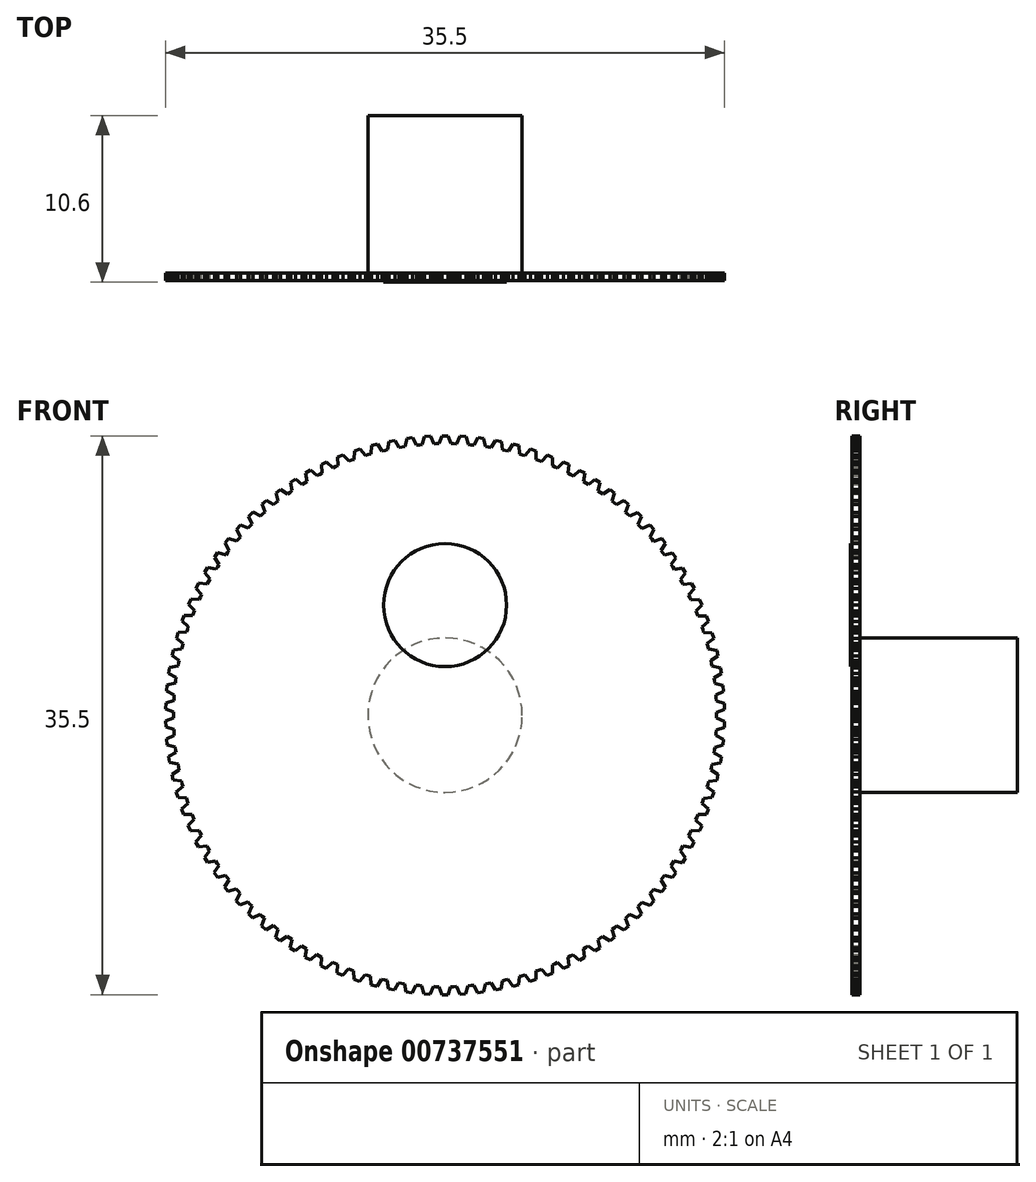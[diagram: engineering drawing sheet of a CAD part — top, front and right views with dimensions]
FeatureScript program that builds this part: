
annotation { "Feature Type Name" : "Feature", "Feature Type Description" : "" }
export const myFeature = defineFeature(function(context is Context, id is Id, definition is map)
    precondition{}
    {
        {
            var Q0;
            Q0=qCreatedBy(makeId("Front.planeOp"),FACE);
            var sketch = newSketch(context, id + "F0", { "sketchPlane" : qUnion([Q0])});
            skLineSegment(sketch, "E0", {"start": v(0, 0) * mm, "end": v(0, 17.75) * mm, "construction": true});
            skCircle(sketch, "E1.0", {"center": v(-0.16, 0) * mm, "radius": 17.25 * mm, "construction": true});
            skLineSegment(sketch, "E2", {"start": v(0, 17.75) * mm, "end": v(-0.19, 17.75) * mm});
            skLineSegment(sketch, "E3", {"start": v(-0.19, 17.75) * mm, "end": v(-0.37, 17.25) * mm});
            skLineSegment(sketch, "E4", {"start": v(-0.37, 17.25) * mm, "end": v(-0.56, 17.24) * mm});
            skLineSegment(sketch, "E5.MirrorCS", {"start": v(0.19, 17.75) * mm, "end": v(0.37, 17.25) * mm});
            skLineSegment(sketch, "E6.MirrorCS", {"start": v(0.37, 17.25) * mm, "end": v(0.56, 17.24) * mm});
            skLineSegment(sketch, "E7.MirrorCS", {"start": v(0, 17.75) * mm, "end": v(0.19, 17.75) * mm});
            skLineSegment(sketch, "E8.1.0", {"start": v(0.95, 17.73) * mm, "end": v(0.73, 17.23) * mm});
            skLineSegment(sketch, "E8.1.1", {"start": v(1.32, 17.7) * mm, "end": v(1.48, 17.19) * mm});
            skLineSegment(sketch, "E8.1.2", {"start": v(1.48, 17.19) * mm, "end": v(1.66, 17.17) * mm});
            skLineSegment(sketch, "E8.1.3", {"start": v(0.73, 17.23) * mm, "end": v(0.55, 17.24) * mm});
            skLineSegment(sketch, "E8.1.4", {"start": v(1.14, 17.71) * mm, "end": v(1.32, 17.7) * mm});
            skLineSegment(sketch, "E8.1.5", {"start": v(1.14, 17.71) * mm, "end": v(0.95, 17.73) * mm});
            skLineSegment(sketch, "E8.2.0", {"start": v(2.09, 17.63) * mm, "end": v(1.84, 17.15) * mm});
            skLineSegment(sketch, "E8.2.1", {"start": v(2.45, 17.58) * mm, "end": v(2.57, 17.06) * mm});
            skLineSegment(sketch, "E8.2.2", {"start": v(2.57, 17.06) * mm, "end": v(2.76, 17.03) * mm});
            skLineSegment(sketch, "E8.2.3", {"start": v(1.84, 17.15) * mm, "end": v(1.65, 17.17) * mm});
            skLineSegment(sketch, "E8.2.4", {"start": v(2.27, 17.6) * mm, "end": v(2.45, 17.58) * mm});
            skLineSegment(sketch, "E8.2.5", {"start": v(2.27, 17.6) * mm, "end": v(2.09, 17.63) * mm});
            skLineSegment(sketch, "E8.3.0", {"start": v(3.21, 17.46) * mm, "end": v(2.93, 17) * mm});
            skLineSegment(sketch, "E8.3.1", {"start": v(3.58, 17.39) * mm, "end": v(3.66, 16.86) * mm});
            skLineSegment(sketch, "E8.3.2", {"start": v(3.66, 16.86) * mm, "end": v(3.84, 16.82) * mm});
            skLineSegment(sketch, "E8.3.3", {"start": v(2.93, 17) * mm, "end": v(2.75, 17.03) * mm});
            skLineSegment(sketch, "E8.3.4", {"start": v(3.4, 17.42) * mm, "end": v(3.58, 17.39) * mm});
            skLineSegment(sketch, "E8.3.5", {"start": v(3.4, 17.42) * mm, "end": v(3.21, 17.46) * mm});
            skLineSegment(sketch, "E8.4.0", {"start": v(4.32, 17.22) * mm, "end": v(4.02, 16.78) * mm});
            skLineSegment(sketch, "E8.4.1", {"start": v(4.68, 17.12) * mm, "end": v(4.73, 16.59) * mm});
            skLineSegment(sketch, "E8.4.2", {"start": v(4.73, 16.59) * mm, "end": v(4.91, 16.54) * mm});
            skLineSegment(sketch, "E8.4.3", {"start": v(4.02, 16.78) * mm, "end": v(3.84, 16.82) * mm});
            skLineSegment(sketch, "E8.4.4", {"start": v(4.5, 17.17) * mm, "end": v(4.68, 17.12) * mm});
            skLineSegment(sketch, "E8.4.5", {"start": v(4.5, 17.17) * mm, "end": v(4.32, 17.22) * mm});
            skLineSegment(sketch, "E8.5.0", {"start": v(5.42, 16.9) * mm, "end": v(5.08, 16.48) * mm});
            skLineSegment(sketch, "E8.5.1", {"start": v(5.77, 16.79) * mm, "end": v(5.79, 16.25) * mm});
            skLineSegment(sketch, "E8.5.2", {"start": v(5.79, 16.25) * mm, "end": v(5.96, 16.19) * mm});
            skLineSegment(sketch, "E8.5.3", {"start": v(5.08, 16.48) * mm, "end": v(4.9, 16.54) * mm});
            skLineSegment(sketch, "E8.5.4", {"start": v(5.6, 16.85) * mm, "end": v(5.77, 16.79) * mm});
            skLineSegment(sketch, "E8.5.5", {"start": v(5.6, 16.85) * mm, "end": v(5.42, 16.9) * mm});
            skLineSegment(sketch, "E8.6.0", {"start": v(6.5, 16.52) * mm, "end": v(6.13, 16.12) * mm});
            skLineSegment(sketch, "E8.6.1", {"start": v(6.83, 16.38) * mm, "end": v(6.82, 15.85) * mm});
            skLineSegment(sketch, "E8.6.2", {"start": v(6.82, 15.85) * mm, "end": v(6.99, 15.77) * mm});
            skLineSegment(sketch, "E8.6.3", {"start": v(6.13, 16.12) * mm, "end": v(5.96, 16.2) * mm});
            skLineSegment(sketch, "E8.6.4", {"start": v(6.66, 16.45) * mm, "end": v(6.83, 16.38) * mm});
            skLineSegment(sketch, "E8.6.5", {"start": v(6.66, 16.45) * mm, "end": v(6.5, 16.52) * mm});
            skLineSegment(sketch, "E8.7.0", {"start": v(7.54, 16.07) * mm, "end": v(7.15, 15.7) * mm});
            skLineSegment(sketch, "E8.7.1", {"start": v(7.87, 15.91) * mm, "end": v(7.82, 15.38) * mm});
            skLineSegment(sketch, "E8.7.2", {"start": v(7.82, 15.38) * mm, "end": v(7.99, 15.3) * mm});
            skLineSegment(sketch, "E8.7.3", {"start": v(7.15, 15.7) * mm, "end": v(6.98, 15.78) * mm});
            skLineSegment(sketch, "E8.7.4", {"start": v(7.7, 16) * mm, "end": v(7.87, 15.91) * mm});
            skLineSegment(sketch, "E8.7.5", {"start": v(7.7, 16) * mm, "end": v(7.54, 16.07) * mm});
            skLineSegment(sketch, "E8.8.0", {"start": v(8.55, 15.56) * mm, "end": v(8.14, 15.2) * mm});
            skLineSegment(sketch, "E8.8.1", {"start": v(8.87, 15.37) * mm, "end": v(8.79, 14.84) * mm});
            skLineSegment(sketch, "E8.8.2", {"start": v(8.79, 14.84) * mm, "end": v(8.95, 14.75) * mm});
            skLineSegment(sketch, "E8.8.3", {"start": v(8.14, 15.2) * mm, "end": v(7.98, 15.3) * mm});
            skLineSegment(sketch, "E8.8.4", {"start": v(8.71, 15.46) * mm, "end": v(8.87, 15.37) * mm});
            skLineSegment(sketch, "E8.8.5", {"start": v(8.71, 15.46) * mm, "end": v(8.55, 15.56) * mm});
            skLineSegment(sketch, "E8.9.0", {"start": v(9.53, 14.98) * mm, "end": v(9.1, 14.66) * mm});
            skLineSegment(sketch, "E8.9.1", {"start": v(9.84, 14.77) * mm, "end": v(9.72, 14.25) * mm});
            skLineSegment(sketch, "E8.9.2", {"start": v(9.72, 14.25) * mm, "end": v(9.88, 14.15) * mm});
            skLineSegment(sketch, "E8.9.3", {"start": v(9.1, 14.66) * mm, "end": v(8.94, 14.75) * mm});
            skLineSegment(sketch, "E8.9.4", {"start": v(9.69, 14.87) * mm, "end": v(9.84, 14.77) * mm});
            skLineSegment(sketch, "E8.9.5", {"start": v(9.69, 14.87) * mm, "end": v(9.53, 14.98) * mm});
            skLineSegment(sketch, "E8.10.0", {"start": v(10.47, 14.33) * mm, "end": v(10.02, 14.04) * mm});
            skLineSegment(sketch, "E8.10.1", {"start": v(10.77, 14.11) * mm, "end": v(10.61, 13.6) * mm});
            skLineSegment(sketch, "E8.10.2", {"start": v(10.61, 13.6) * mm, "end": v(10.76, 13.48) * mm});
            skLineSegment(sketch, "E8.10.3", {"start": v(10.02, 14.04) * mm, "end": v(9.87, 14.15) * mm});
            skLineSegment(sketch, "E8.10.4", {"start": v(10.62, 14.22) * mm, "end": v(10.77, 14.11) * mm});
            skLineSegment(sketch, "E8.10.5", {"start": v(10.62, 14.22) * mm, "end": v(10.47, 14.33) * mm});
            skLineSegment(sketch, "E8.11.0", {"start": v(11.37, 13.63) * mm, "end": v(10.9, 13.37) * mm});
            skLineSegment(sketch, "E8.11.1", {"start": v(11.65, 13.4) * mm, "end": v(11.46, 12.89) * mm});
            skLineSegment(sketch, "E8.11.2", {"start": v(11.46, 12.89) * mm, "end": v(11.6, 12.77) * mm});
            skLineSegment(sketch, "E8.11.3", {"start": v(10.9, 13.37) * mm, "end": v(10.75, 13.49) * mm});
            skLineSegment(sketch, "E8.11.4", {"start": v(11.5, 13.51) * mm, "end": v(11.65, 13.4) * mm});
            skLineSegment(sketch, "E8.11.5", {"start": v(11.5, 13.51) * mm, "end": v(11.37, 13.63) * mm});
            skLineSegment(sketch, "E8.12.0", {"start": v(12.22, 12.88) * mm, "end": v(11.73, 12.65) * mm});
            skLineSegment(sketch, "E8.12.1", {"start": v(12.48, 12.62) * mm, "end": v(12.27, 12.13) * mm});
            skLineSegment(sketch, "E8.12.2", {"start": v(12.27, 12.13) * mm, "end": v(12.4, 12) * mm});
            skLineSegment(sketch, "E8.12.3", {"start": v(11.73, 12.65) * mm, "end": v(11.6, 12.77) * mm});
            skLineSegment(sketch, "E8.12.4", {"start": v(12.35, 12.75) * mm, "end": v(12.48, 12.62) * mm});
            skLineSegment(sketch, "E8.12.5", {"start": v(12.35, 12.75) * mm, "end": v(12.22, 12.88) * mm});
            skLineSegment(sketch, "E8.13.0", {"start": v(13.02, 12.07) * mm, "end": v(12.52, 11.87) * mm});
            skLineSegment(sketch, "E8.13.1", {"start": v(13.27, 11.8) * mm, "end": v(13.02, 11.32) * mm});
            skLineSegment(sketch, "E8.13.2", {"start": v(13.02, 11.32) * mm, "end": v(13.14, 11.18) * mm});
            skLineSegment(sketch, "E8.13.3", {"start": v(12.52, 11.87) * mm, "end": v(12.4, 12) * mm});
            skLineSegment(sketch, "E8.13.4", {"start": v(13.14, 11.93) * mm, "end": v(13.27, 11.8) * mm});
            skLineSegment(sketch, "E8.13.5", {"start": v(13.14, 11.93) * mm, "end": v(13.02, 12.07) * mm});
            skLineSegment(sketch, "E8.14.0", {"start": v(13.76, 11.2) * mm, "end": v(13.25, 11.04) * mm});
            skLineSegment(sketch, "E8.14.1", {"start": v(14, 10.92) * mm, "end": v(13.72, 10.46) * mm});
            skLineSegment(sketch, "E8.14.2", {"start": v(13.72, 10.46) * mm, "end": v(13.83, 10.31) * mm});
            skLineSegment(sketch, "E8.14.3", {"start": v(13.25, 11.04) * mm, "end": v(13.14, 11.18) * mm});
            skLineSegment(sketch, "E8.14.4", {"start": v(13.88, 11.06) * mm, "end": v(14, 10.92) * mm});
            skLineSegment(sketch, "E8.14.5", {"start": v(13.88, 11.06) * mm, "end": v(13.76, 11.2) * mm});
            skLineSegment(sketch, "E8.15.0", {"start": v(14.45, 10.3) * mm, "end": v(13.93, 10.17) * mm});
            skLineSegment(sketch, "E8.15.1", {"start": v(14.67, 10) * mm, "end": v(14.36, 9.56) * mm});
            skLineSegment(sketch, "E8.15.2", {"start": v(14.36, 9.56) * mm, "end": v(14.46, 9.4) * mm});
            skLineSegment(sketch, "E8.15.3", {"start": v(13.93, 10.17) * mm, "end": v(13.82, 10.32) * mm});
            skLineSegment(sketch, "E8.15.4", {"start": v(14.56, 10.15) * mm, "end": v(14.67, 10) * mm});
            skLineSegment(sketch, "E8.15.5", {"start": v(14.56, 10.15) * mm, "end": v(14.45, 10.3) * mm});
            skLineSegment(sketch, "E8.16.0", {"start": v(15.08, 9.36) * mm, "end": v(14.56, 9.26) * mm});
            skLineSegment(sketch, "E8.16.1", {"start": v(15.28, 9.04) * mm, "end": v(14.94, 8.62) * mm});
            skLineSegment(sketch, "E8.16.2", {"start": v(14.94, 8.62) * mm, "end": v(15.04, 8.46) * mm});
            skLineSegment(sketch, "E8.16.3", {"start": v(14.56, 9.26) * mm, "end": v(14.46, 9.41) * mm});
            skLineSegment(sketch, "E8.16.4", {"start": v(15.18, 9.2) * mm, "end": v(15.28, 9.04) * mm});
            skLineSegment(sketch, "E8.16.5", {"start": v(15.18, 9.2) * mm, "end": v(15.08, 9.36) * mm});
            skLineSegment(sketch, "E8.17.0", {"start": v(15.65, 8.37) * mm, "end": v(15.12, 8.3) * mm});
            skLineSegment(sketch, "E8.17.1", {"start": v(15.82, 8.04) * mm, "end": v(15.46, 7.64) * mm});
            skLineSegment(sketch, "E8.17.2", {"start": v(15.46, 7.64) * mm, "end": v(15.55, 7.48) * mm});
            skLineSegment(sketch, "E8.17.3", {"start": v(15.12, 8.3) * mm, "end": v(15.03, 8.47) * mm});
            skLineSegment(sketch, "E8.17.4", {"start": v(15.74, 8.2) * mm, "end": v(15.82, 8.04) * mm});
            skLineSegment(sketch, "E8.17.5", {"start": v(15.74, 8.2) * mm, "end": v(15.65, 8.37) * mm});
            skLineSegment(sketch, "E8.18.0", {"start": v(16.16, 7.35) * mm, "end": v(15.62, 7.32) * mm});
            skLineSegment(sketch, "E8.18.1", {"start": v(16.3, 7.01) * mm, "end": v(15.92, 6.64) * mm});
            skLineSegment(sketch, "E8.18.2", {"start": v(15.92, 6.64) * mm, "end": v(16, 6.47) * mm});
            skLineSegment(sketch, "E8.18.3", {"start": v(15.62, 7.32) * mm, "end": v(15.54, 7.49) * mm});
            skLineSegment(sketch, "E8.18.4", {"start": v(16.23, 7.18) * mm, "end": v(16.3, 7.01) * mm});
            skLineSegment(sketch, "E8.18.5", {"start": v(16.23, 7.18) * mm, "end": v(16.16, 7.35) * mm});
            skLineSegment(sketch, "E8.19.0", {"start": v(16.6, 6.3) * mm, "end": v(16.06, 6.3) * mm});
            skLineSegment(sketch, "E8.19.1", {"start": v(16.72, 5.95) * mm, "end": v(16.31, 5.6) * mm});
            skLineSegment(sketch, "E8.19.2", {"start": v(16.31, 5.6) * mm, "end": v(16.38, 5.43) * mm});
            skLineSegment(sketch, "E8.19.3", {"start": v(16.06, 6.3) * mm, "end": v(16, 6.47) * mm});
            skLineSegment(sketch, "E8.19.4", {"start": v(16.66, 6.13) * mm, "end": v(16.72, 5.95) * mm});
            skLineSegment(sketch, "E8.19.5", {"start": v(16.66, 6.13) * mm, "end": v(16.6, 6.3) * mm});
            skLineSegment(sketch, "E8.20.0", {"start": v(16.96, 5.22) * mm, "end": v(16.43, 5.26) * mm});
            skLineSegment(sketch, "E8.20.1", {"start": v(17.07, 4.87) * mm, "end": v(16.64, 4.55) * mm});
            skLineSegment(sketch, "E8.20.2", {"start": v(16.64, 4.55) * mm, "end": v(16.69, 4.37) * mm});
            skLineSegment(sketch, "E8.20.3", {"start": v(16.43, 5.26) * mm, "end": v(16.37, 5.44) * mm});
            skLineSegment(sketch, "E8.20.4", {"start": v(17.02, 5.05) * mm, "end": v(17.07, 4.87) * mm});
            skLineSegment(sketch, "E8.20.5", {"start": v(17.02, 5.05) * mm, "end": v(16.96, 5.22) * mm});
            skLineSegment(sketch, "E8.21.0", {"start": v(17.26, 4.13) * mm, "end": v(16.73, 4.2) * mm});
            skLineSegment(sketch, "E8.21.1", {"start": v(17.35, 3.76) * mm, "end": v(16.9, 3.47) * mm});
            skLineSegment(sketch, "E8.21.2", {"start": v(16.9, 3.47) * mm, "end": v(16.94, 3.29) * mm});
            skLineSegment(sketch, "E8.21.3", {"start": v(16.73, 4.2) * mm, "end": v(16.69, 4.38) * mm});
            skLineSegment(sketch, "E8.21.4", {"start": v(17.3, 3.94) * mm, "end": v(17.35, 3.76) * mm});
            skLineSegment(sketch, "E8.21.5", {"start": v(17.3, 3.94) * mm, "end": v(17.26, 4.13) * mm});
            skLineSegment(sketch, "E8.22.0", {"start": v(17.5, 3.01) * mm, "end": v(16.97, 3.11) * mm});
            skLineSegment(sketch, "E8.22.1", {"start": v(17.55, 2.64) * mm, "end": v(17.08, 2.38) * mm});
            skLineSegment(sketch, "E8.22.2", {"start": v(17.08, 2.38) * mm, "end": v(17.11, 2.2) * mm});
            skLineSegment(sketch, "E8.22.3", {"start": v(16.97, 3.11) * mm, "end": v(16.93, 3.3) * mm});
            skLineSegment(sketch, "E8.22.4", {"start": v(17.52, 2.83) * mm, "end": v(17.55, 2.64) * mm});
            skLineSegment(sketch, "E8.22.5", {"start": v(17.52, 2.83) * mm, "end": v(17.5, 3.01) * mm});
            skLineSegment(sketch, "E8.23.0", {"start": v(17.65, 1.88) * mm, "end": v(17.13, 2.02) * mm});
            skLineSegment(sketch, "E8.23.1", {"start": v(17.69, 1.51) * mm, "end": v(17.2, 1.28) * mm});
            skLineSegment(sketch, "E8.23.2", {"start": v(17.2, 1.28) * mm, "end": v(17.22, 1.1) * mm});
            skLineSegment(sketch, "E8.23.3", {"start": v(17.13, 2.02) * mm, "end": v(17.11, 2.2) * mm});
            skLineSegment(sketch, "E8.23.4", {"start": v(17.67, 1.7) * mm, "end": v(17.69, 1.51) * mm});
            skLineSegment(sketch, "E8.23.5", {"start": v(17.67, 1.7) * mm, "end": v(17.65, 1.88) * mm});
            skLineSegment(sketch, "E8.24.0", {"start": v(17.74, 0.75) * mm, "end": v(17.23, 0.92) * mm});
            skLineSegment(sketch, "E8.24.1", {"start": v(17.75, 0.38) * mm, "end": v(17.25, 0.18) * mm});
            skLineSegment(sketch, "E8.24.2", {"start": v(17.25, 0.18) * mm, "end": v(17.25, -0.01) * mm});
            skLineSegment(sketch, "E8.24.3", {"start": v(17.23, 0.92) * mm, "end": v(17.22, 1.1) * mm});
            skLineSegment(sketch, "E8.24.4", {"start": v(17.74, 0.56) * mm, "end": v(17.75, 0.38) * mm});
            skLineSegment(sketch, "E8.24.5", {"start": v(17.74, 0.56) * mm, "end": v(17.74, 0.75) * mm});
            skLineSegment(sketch, "E8.25.0", {"start": v(17.75, -0.39) * mm, "end": v(17.25, -0.19) * mm});
            skLineSegment(sketch, "E8.25.1", {"start": v(17.73, -0.76) * mm, "end": v(17.22, -0.93) * mm});
            skLineSegment(sketch, "E8.25.2", {"start": v(17.22, -0.93) * mm, "end": v(17.22, -1.12) * mm});
            skLineSegment(sketch, "E8.25.3", {"start": v(17.25, -0.19) * mm, "end": v(17.25, 0) * mm});
            skLineSegment(sketch, "E8.25.4", {"start": v(17.74, -0.57) * mm, "end": v(17.73, -0.76) * mm});
            skLineSegment(sketch, "E8.25.5", {"start": v(17.74, -0.57) * mm, "end": v(17.75, -0.39) * mm});
            skLineSegment(sketch, "E8.26.0", {"start": v(17.69, -1.53) * mm, "end": v(17.2, -1.3) * mm});
            skLineSegment(sketch, "E8.26.1", {"start": v(17.65, -1.9) * mm, "end": v(17.13, -2.03) * mm});
            skLineSegment(sketch, "E8.26.2", {"start": v(17.13, -2.03) * mm, "end": v(17.1, -2.22) * mm});
            skLineSegment(sketch, "E8.26.3", {"start": v(17.2, -1.3) * mm, "end": v(17.22, -1.1) * mm});
            skLineSegment(sketch, "E8.26.4", {"start": v(17.67, -1.71) * mm, "end": v(17.65, -1.9) * mm});
            skLineSegment(sketch, "E8.26.5", {"start": v(17.67, -1.71) * mm, "end": v(17.69, -1.53) * mm});
            skLineSegment(sketch, "E8.27.0", {"start": v(17.55, -2.66) * mm, "end": v(17.08, -2.4) * mm});
            skLineSegment(sketch, "E8.27.1", {"start": v(17.5, -3.02) * mm, "end": v(16.96, -3.13) * mm});
            skLineSegment(sketch, "E8.27.2", {"start": v(16.96, -3.13) * mm, "end": v(16.93, -3.3) * mm});
            skLineSegment(sketch, "E8.27.3", {"start": v(17.08, -2.4) * mm, "end": v(17.1, -2.2) * mm});
            skLineSegment(sketch, "E8.27.4", {"start": v(17.52, -2.84) * mm, "end": v(17.5, -3.02) * mm});
            skLineSegment(sketch, "E8.27.5", {"start": v(17.52, -2.84) * mm, "end": v(17.55, -2.66) * mm});
            skLineSegment(sketch, "E8.28.0", {"start": v(17.34, -3.77) * mm, "end": v(16.9, -3.48) * mm});
            skLineSegment(sketch, "E8.28.1", {"start": v(17.26, -4.14) * mm, "end": v(16.73, -4.2) * mm});
            skLineSegment(sketch, "E8.28.2", {"start": v(16.73, -4.2) * mm, "end": v(16.68, -4.39) * mm});
            skLineSegment(sketch, "E8.28.3", {"start": v(16.9, -3.48) * mm, "end": v(16.93, -3.3) * mm});
            skLineSegment(sketch, "E8.28.4", {"start": v(17.3, -3.96) * mm, "end": v(17.26, -4.14) * mm});
            skLineSegment(sketch, "E8.28.5", {"start": v(17.3, -3.96) * mm, "end": v(17.34, -3.77) * mm});
            skLineSegment(sketch, "E8.29.0", {"start": v(17.07, -4.88) * mm, "end": v(16.64, -4.56) * mm});
            skLineSegment(sketch, "E8.29.1", {"start": v(16.96, -5.24) * mm, "end": v(16.43, -5.27) * mm});
            skLineSegment(sketch, "E8.29.2", {"start": v(16.43, -5.27) * mm, "end": v(16.37, -5.45) * mm});
            skLineSegment(sketch, "E8.29.3", {"start": v(16.64, -4.56) * mm, "end": v(16.69, -4.38) * mm});
            skLineSegment(sketch, "E8.29.4", {"start": v(17.01, -5.06) * mm, "end": v(16.96, -5.24) * mm});
            skLineSegment(sketch, "E8.29.5", {"start": v(17.01, -5.06) * mm, "end": v(17.07, -4.88) * mm});
            skLineSegment(sketch, "E8.30.0", {"start": v(16.72, -5.96) * mm, "end": v(16.31, -5.61) * mm});
            skLineSegment(sketch, "E8.30.1", {"start": v(16.6, -6.31) * mm, "end": v(16.05, -6.31) * mm});
            skLineSegment(sketch, "E8.30.2", {"start": v(16.05, -6.31) * mm, "end": v(15.99, -6.48) * mm});
            skLineSegment(sketch, "E8.30.3", {"start": v(16.31, -5.61) * mm, "end": v(16.37, -5.44) * mm});
            skLineSegment(sketch, "E8.30.4", {"start": v(16.66, -6.14) * mm, "end": v(16.6, -6.31) * mm});
            skLineSegment(sketch, "E8.30.5", {"start": v(16.66, -6.14) * mm, "end": v(16.72, -5.96) * mm});
            skLineSegment(sketch, "E8.31.0", {"start": v(16.3, -7.02) * mm, "end": v(15.92, -6.65) * mm});
            skLineSegment(sketch, "E8.31.1", {"start": v(16.15, -7.36) * mm, "end": v(15.62, -7.33) * mm});
            skLineSegment(sketch, "E8.31.2", {"start": v(15.62, -7.33) * mm, "end": v(15.54, -7.5) * mm});
            skLineSegment(sketch, "E8.31.3", {"start": v(15.92, -6.65) * mm, "end": v(15.99, -6.48) * mm});
            skLineSegment(sketch, "E8.31.4", {"start": v(16.23, -7.2) * mm, "end": v(16.15, -7.36) * mm});
            skLineSegment(sketch, "E8.31.5", {"start": v(16.23, -7.2) * mm, "end": v(16.3, -7.02) * mm});
            skLineSegment(sketch, "E8.32.0", {"start": v(15.82, -8.05) * mm, "end": v(15.46, -7.65) * mm});
            skLineSegment(sketch, "E8.32.1", {"start": v(15.65, -8.38) * mm, "end": v(15.11, -8.31) * mm});
            skLineSegment(sketch, "E8.32.2", {"start": v(15.11, -8.31) * mm, "end": v(15.03, -8.48) * mm});
            skLineSegment(sketch, "E8.32.3", {"start": v(15.46, -7.65) * mm, "end": v(15.54, -7.49) * mm});
            skLineSegment(sketch, "E8.32.4", {"start": v(15.73, -8.22) * mm, "end": v(15.65, -8.38) * mm});
            skLineSegment(sketch, "E8.32.5", {"start": v(15.73, -8.22) * mm, "end": v(15.82, -8.05) * mm});
            skLineSegment(sketch, "E8.33.0", {"start": v(15.27, -9.05) * mm, "end": v(14.94, -8.63) * mm});
            skLineSegment(sketch, "E8.33.1", {"start": v(15.08, -9.37) * mm, "end": v(14.55, -9.26) * mm});
            skLineSegment(sketch, "E8.33.2", {"start": v(14.55, -9.26) * mm, "end": v(14.45, -9.42) * mm});
            skLineSegment(sketch, "E8.33.3", {"start": v(14.94, -8.63) * mm, "end": v(15.03, -8.47) * mm});
            skLineSegment(sketch, "E8.33.4", {"start": v(15.17, -9.2) * mm, "end": v(15.08, -9.37) * mm});
            skLineSegment(sketch, "E8.33.5", {"start": v(15.17, -9.2) * mm, "end": v(15.27, -9.05) * mm});
            skLineSegment(sketch, "E8.34.0", {"start": v(14.66, -10) * mm, "end": v(14.35, -9.57) * mm});
            skLineSegment(sketch, "E8.34.1", {"start": v(14.45, -10.31) * mm, "end": v(13.93, -10.18) * mm});
            skLineSegment(sketch, "E8.34.2", {"start": v(13.93, -10.18) * mm, "end": v(13.82, -10.33) * mm});
            skLineSegment(sketch, "E8.34.3", {"start": v(14.35, -9.57) * mm, "end": v(14.46, -9.41) * mm});
            skLineSegment(sketch, "E8.34.4", {"start": v(14.55, -10.16) * mm, "end": v(14.45, -10.31) * mm});
            skLineSegment(sketch, "E8.34.5", {"start": v(14.55, -10.16) * mm, "end": v(14.66, -10) * mm});
            skLineSegment(sketch, "E8.35.0", {"start": v(13.99, -10.93) * mm, "end": v(13.71, -10.47) * mm});
            skLineSegment(sketch, "E8.35.1", {"start": v(13.76, -11.22) * mm, "end": v(13.25, -11.05) * mm});
            skLineSegment(sketch, "E8.35.2", {"start": v(13.25, -11.05) * mm, "end": v(13.13, -11.2) * mm});
            skLineSegment(sketch, "E8.35.3", {"start": v(13.71, -10.47) * mm, "end": v(13.82, -10.32) * mm});
            skLineSegment(sketch, "E8.35.4", {"start": v(13.87, -11.07) * mm, "end": v(13.76, -11.22) * mm});
            skLineSegment(sketch, "E8.35.5", {"start": v(13.87, -11.07) * mm, "end": v(13.99, -10.93) * mm});
            skLineSegment(sketch, "E8.36.0", {"start": v(13.26, -11.8) * mm, "end": v(13.01, -11.33) * mm});
            skLineSegment(sketch, "E8.36.1", {"start": v(13, -12.08) * mm, "end": v(12.51, -11.88) * mm});
            skLineSegment(sketch, "E8.36.2", {"start": v(12.51, -11.88) * mm, "end": v(12.38, -12.01) * mm});
            skLineSegment(sketch, "E8.36.3", {"start": v(13.01, -11.33) * mm, "end": v(13.13, -11.19) * mm});
            skLineSegment(sketch, "E8.36.4", {"start": v(13.13, -11.94) * mm, "end": v(13, -12.08) * mm});
            skLineSegment(sketch, "E8.36.5", {"start": v(13.13, -11.94) * mm, "end": v(13.26, -11.8) * mm});
            skLineSegment(sketch, "E8.37.0", {"start": v(12.48, -12.63) * mm, "end": v(12.26, -12.14) * mm});
            skLineSegment(sketch, "E8.37.1", {"start": v(12.2, -12.89) * mm, "end": v(11.72, -12.65) * mm});
            skLineSegment(sketch, "E8.37.2", {"start": v(11.72, -12.65) * mm, "end": v(11.59, -12.78) * mm});
            skLineSegment(sketch, "E8.37.3", {"start": v(12.26, -12.14) * mm, "end": v(12.4, -12) * mm});
            skLineSegment(sketch, "E8.37.4", {"start": v(12.34, -12.76) * mm, "end": v(12.2, -12.89) * mm});
            skLineSegment(sketch, "E8.37.5", {"start": v(12.34, -12.76) * mm, "end": v(12.48, -12.63) * mm});
            skLineSegment(sketch, "E8.38.0", {"start": v(11.64, -13.4) * mm, "end": v(11.46, -12.9) * mm});
            skLineSegment(sketch, "E8.38.1", {"start": v(11.36, -13.64) * mm, "end": v(10.89, -13.38) * mm});
            skLineSegment(sketch, "E8.38.2", {"start": v(10.89, -13.38) * mm, "end": v(10.75, -13.5) * mm});
            skLineSegment(sketch, "E8.38.3", {"start": v(11.46, -12.9) * mm, "end": v(11.6, -12.77) * mm});
            skLineSegment(sketch, "E8.38.4", {"start": v(11.5, -13.52) * mm, "end": v(11.36, -13.64) * mm});
            skLineSegment(sketch, "E8.38.5", {"start": v(11.5, -13.52) * mm, "end": v(11.64, -13.4) * mm});
            skLineSegment(sketch, "E8.39.0", {"start": v(10.76, -14.12) * mm, "end": v(10.6, -13.6) * mm});
            skLineSegment(sketch, "E8.39.1", {"start": v(10.46, -14.34) * mm, "end": v(10, -14.05) * mm});
            skLineSegment(sketch, "E8.39.2", {"start": v(10, -14.05) * mm, "end": v(9.86, -14.16) * mm});
            skLineSegment(sketch, "E8.39.3", {"start": v(10.6, -13.6) * mm, "end": v(10.75, -13.5) * mm});
            skLineSegment(sketch, "E8.39.4", {"start": v(10.6, -14.23) * mm, "end": v(10.46, -14.34) * mm});
            skLineSegment(sketch, "E8.39.5", {"start": v(10.6, -14.23) * mm, "end": v(10.76, -14.12) * mm});
            skLineSegment(sketch, "E8.40.0", {"start": v(9.83, -14.78) * mm, "end": v(9.71, -14.26) * mm});
            skLineSegment(sketch, "E8.40.1", {"start": v(9.52, -14.98) * mm, "end": v(9.09, -14.66) * mm});
            skLineSegment(sketch, "E8.40.2", {"start": v(9.09, -14.66) * mm, "end": v(8.93, -14.76) * mm});
            skLineSegment(sketch, "E8.40.3", {"start": v(9.71, -14.26) * mm, "end": v(9.87, -14.15) * mm});
            skLineSegment(sketch, "E8.40.4", {"start": v(9.68, -14.88) * mm, "end": v(9.52, -14.98) * mm});
            skLineSegment(sketch, "E8.40.5", {"start": v(9.68, -14.88) * mm, "end": v(9.83, -14.78) * mm});
            skLineSegment(sketch, "E8.41.0", {"start": v(8.86, -15.38) * mm, "end": v(8.78, -14.85) * mm});
            skLineSegment(sketch, "E8.41.1", {"start": v(8.54, -15.56) * mm, "end": v(8.13, -15.21) * mm});
            skLineSegment(sketch, "E8.41.2", {"start": v(8.13, -15.21) * mm, "end": v(7.97, -15.3) * mm});
            skLineSegment(sketch, "E8.41.3", {"start": v(8.78, -14.85) * mm, "end": v(8.94, -14.76) * mm});
            skLineSegment(sketch, "E8.41.4", {"start": v(8.7, -15.47) * mm, "end": v(8.54, -15.56) * mm});
            skLineSegment(sketch, "E8.41.5", {"start": v(8.7, -15.47) * mm, "end": v(8.86, -15.38) * mm});
            skLineSegment(sketch, "E8.42.0", {"start": v(7.86, -15.92) * mm, "end": v(7.8, -15.38) * mm});
            skLineSegment(sketch, "E8.42.1", {"start": v(7.53, -16.08) * mm, "end": v(7.14, -15.7) * mm});
            skLineSegment(sketch, "E8.42.2", {"start": v(7.14, -15.7) * mm, "end": v(6.97, -15.78) * mm});
            skLineSegment(sketch, "E8.42.3", {"start": v(7.8, -15.38) * mm, "end": v(7.98, -15.3) * mm});
            skLineSegment(sketch, "E8.42.4", {"start": v(7.7, -16) * mm, "end": v(7.53, -16.08) * mm});
            skLineSegment(sketch, "E8.42.5", {"start": v(7.7, -16) * mm, "end": v(7.86, -15.92) * mm});
            skLineSegment(sketch, "E8.43.0", {"start": v(6.82, -16.39) * mm, "end": v(6.8, -15.85) * mm});
            skLineSegment(sketch, "E8.43.1", {"start": v(6.48, -16.53) * mm, "end": v(6.12, -16.13) * mm});
            skLineSegment(sketch, "E8.43.2", {"start": v(6.12, -16.13) * mm, "end": v(5.94, -16.2) * mm});
            skLineSegment(sketch, "E8.43.3", {"start": v(6.8, -15.85) * mm, "end": v(6.98, -15.78) * mm});
            skLineSegment(sketch, "E8.43.4", {"start": v(6.65, -16.46) * mm, "end": v(6.48, -16.53) * mm});
            skLineSegment(sketch, "E8.43.5", {"start": v(6.65, -16.46) * mm, "end": v(6.82, -16.39) * mm});
            skLineSegment(sketch, "E8.44.0", {"start": v(5.76, -16.8) * mm, "end": v(5.78, -16.25) * mm});
            skLineSegment(sketch, "E8.44.1", {"start": v(5.4, -16.9) * mm, "end": v(5.07, -16.49) * mm});
            skLineSegment(sketch, "E8.44.2", {"start": v(5.07, -16.49) * mm, "end": v(4.9, -16.54) * mm});
            skLineSegment(sketch, "E8.44.3", {"start": v(5.78, -16.25) * mm, "end": v(5.95, -16.2) * mm});
            skLineSegment(sketch, "E8.44.4", {"start": v(5.58, -16.85) * mm, "end": v(5.4, -16.9) * mm});
            skLineSegment(sketch, "E8.44.5", {"start": v(5.58, -16.85) * mm, "end": v(5.76, -16.8) * mm});
            skLineSegment(sketch, "E8.45.0", {"start": v(4.67, -17.13) * mm, "end": v(4.72, -16.6) * mm});
            skLineSegment(sketch, "E8.45.1", {"start": v(4.31, -17.22) * mm, "end": v(4, -16.78) * mm});
            skLineSegment(sketch, "E8.45.2", {"start": v(4, -16.78) * mm, "end": v(3.82, -16.82) * mm});
            skLineSegment(sketch, "E8.45.3", {"start": v(4.72, -16.6) * mm, "end": v(4.9, -16.54) * mm});
            skLineSegment(sketch, "E8.45.4", {"start": v(4.5, -17.17) * mm, "end": v(4.31, -17.22) * mm});
            skLineSegment(sketch, "E8.45.5", {"start": v(4.5, -17.17) * mm, "end": v(4.67, -17.13) * mm});
            skLineSegment(sketch, "E8.46.0", {"start": v(3.56, -17.39) * mm, "end": v(3.65, -16.86) * mm});
            skLineSegment(sketch, "E8.46.1", {"start": v(3.2, -17.46) * mm, "end": v(2.92, -17) * mm});
            skLineSegment(sketch, "E8.46.2", {"start": v(2.92, -17) * mm, "end": v(2.74, -17.03) * mm});
            skLineSegment(sketch, "E8.46.3", {"start": v(3.65, -16.86) * mm, "end": v(3.83, -16.82) * mm});
            skLineSegment(sketch, "E8.46.4", {"start": v(3.38, -17.42) * mm, "end": v(3.2, -17.46) * mm});
            skLineSegment(sketch, "E8.46.5", {"start": v(3.38, -17.42) * mm, "end": v(3.56, -17.39) * mm});
            skLineSegment(sketch, "E8.47.0", {"start": v(2.44, -17.58) * mm, "end": v(2.56, -17.06) * mm});
            skLineSegment(sketch, "E8.47.1", {"start": v(2.07, -17.63) * mm, "end": v(1.83, -17.15) * mm});
            skLineSegment(sketch, "E8.47.2", {"start": v(1.83, -17.15) * mm, "end": v(1.64, -17.17) * mm});
            skLineSegment(sketch, "E8.47.3", {"start": v(2.56, -17.06) * mm, "end": v(2.75, -17.03) * mm});
            skLineSegment(sketch, "E8.47.4", {"start": v(2.26, -17.6) * mm, "end": v(2.07, -17.63) * mm});
            skLineSegment(sketch, "E8.47.5", {"start": v(2.26, -17.6) * mm, "end": v(2.44, -17.58) * mm});
            skLineSegment(sketch, "E8.48.0", {"start": v(1.31, -17.7) * mm, "end": v(1.47, -17.19) * mm});
            skLineSegment(sketch, "E8.48.1", {"start": v(0.94, -17.73) * mm, "end": v(0.72, -17.23) * mm});
            skLineSegment(sketch, "E8.48.2", {"start": v(0.72, -17.23) * mm, "end": v(0.54, -17.24) * mm});
            skLineSegment(sketch, "E8.48.3", {"start": v(1.47, -17.19) * mm, "end": v(1.65, -17.17) * mm});
            skLineSegment(sketch, "E8.48.4", {"start": v(1.13, -17.71) * mm, "end": v(0.94, -17.73) * mm});
            skLineSegment(sketch, "E8.48.5", {"start": v(1.13, -17.71) * mm, "end": v(1.31, -17.7) * mm});
            skLineSegment(sketch, "E8.49.0", {"start": v(0.17, -17.75) * mm, "end": v(0.36, -17.25) * mm});
            skLineSegment(sketch, "E8.49.1", {"start": v(-0.2, -17.75) * mm, "end": v(-0.38, -17.25) * mm});
            skLineSegment(sketch, "E8.49.2", {"start": v(-0.38, -17.25) * mm, "end": v(-0.57, -17.24) * mm});
            skLineSegment(sketch, "E8.49.3", {"start": v(0.36, -17.25) * mm, "end": v(0.55, -17.24) * mm});
            skLineSegment(sketch, "E8.49.4", {"start": v(-0.01, -17.75) * mm, "end": v(-0.2, -17.75) * mm});
            skLineSegment(sketch, "E8.49.5", {"start": v(-0.01, -17.75) * mm, "end": v(0.17, -17.75) * mm});
            skLineSegment(sketch, "E8.50.0", {"start": v(-0.96, -17.72) * mm, "end": v(-0.75, -17.23) * mm});
            skLineSegment(sketch, "E8.50.1", {"start": v(-1.33, -17.7) * mm, "end": v(-1.49, -17.19) * mm});
            skLineSegment(sketch, "E8.50.2", {"start": v(-1.49, -17.19) * mm, "end": v(-1.67, -17.17) * mm});
            skLineSegment(sketch, "E8.50.3", {"start": v(-0.75, -17.23) * mm, "end": v(-0.56, -17.24) * mm});
            skLineSegment(sketch, "E8.50.4", {"start": v(-1.15, -17.71) * mm, "end": v(-1.33, -17.7) * mm});
            skLineSegment(sketch, "E8.50.5", {"start": v(-1.15, -17.71) * mm, "end": v(-0.96, -17.72) * mm});
            skLineSegment(sketch, "E8.51.0", {"start": v(-2.1, -17.63) * mm, "end": v(-1.85, -17.15) * mm});
            skLineSegment(sketch, "E8.51.1", {"start": v(-2.47, -17.58) * mm, "end": v(-2.59, -17.06) * mm});
            skLineSegment(sketch, "E8.51.2", {"start": v(-2.59, -17.06) * mm, "end": v(-2.77, -17.03) * mm});
            skLineSegment(sketch, "E8.51.3", {"start": v(-1.85, -17.15) * mm, "end": v(-1.66, -17.17) * mm});
            skLineSegment(sketch, "E8.51.4", {"start": v(-2.28, -17.6) * mm, "end": v(-2.47, -17.58) * mm});
            skLineSegment(sketch, "E8.51.5", {"start": v(-2.28, -17.6) * mm, "end": v(-2.1, -17.63) * mm});
            skLineSegment(sketch, "E8.52.0", {"start": v(-3.22, -17.46) * mm, "end": v(-2.94, -17) * mm});
            skLineSegment(sketch, "E8.52.1", {"start": v(-3.59, -17.38) * mm, "end": v(-3.67, -16.85) * mm});
            skLineSegment(sketch, "E8.52.2", {"start": v(-3.67, -16.85) * mm, "end": v(-3.85, -16.82) * mm});
            skLineSegment(sketch, "E8.52.3", {"start": v(-2.94, -17) * mm, "end": v(-2.76, -17.03) * mm});
            skLineSegment(sketch, "E8.52.4", {"start": v(-3.4, -17.42) * mm, "end": v(-3.59, -17.38) * mm});
            skLineSegment(sketch, "E8.52.5", {"start": v(-3.4, -17.42) * mm, "end": v(-3.22, -17.46) * mm});
            skLineSegment(sketch, "E8.53.0", {"start": v(-4.33, -17.21) * mm, "end": v(-4.03, -16.77) * mm});
            skLineSegment(sketch, "E8.53.1", {"start": v(-4.7, -17.12) * mm, "end": v(-4.75, -16.58) * mm});
            skLineSegment(sketch, "E8.53.2", {"start": v(-4.75, -16.58) * mm, "end": v(-4.92, -16.53) * mm});
            skLineSegment(sketch, "E8.53.3", {"start": v(-4.03, -16.77) * mm, "end": v(-3.85, -16.82) * mm});
            skLineSegment(sketch, "E8.53.4", {"start": v(-4.51, -17.17) * mm, "end": v(-4.7, -17.12) * mm});
            skLineSegment(sketch, "E8.53.5", {"start": v(-4.51, -17.17) * mm, "end": v(-4.33, -17.21) * mm});
            skLineSegment(sketch, "E8.54.0", {"start": v(-5.43, -16.9) * mm, "end": v(-5.1, -16.48) * mm});
            skLineSegment(sketch, "E8.54.1", {"start": v(-5.78, -16.78) * mm, "end": v(-5.8, -16.25) * mm});
            skLineSegment(sketch, "E8.54.2", {"start": v(-5.8, -16.25) * mm, "end": v(-5.97, -16.18) * mm});
            skLineSegment(sketch, "E8.54.3", {"start": v(-5.1, -16.48) * mm, "end": v(-4.92, -16.54) * mm});
            skLineSegment(sketch, "E8.54.4", {"start": v(-5.6, -16.84) * mm, "end": v(-5.78, -16.78) * mm});
            skLineSegment(sketch, "E8.54.5", {"start": v(-5.6, -16.84) * mm, "end": v(-5.43, -16.9) * mm});
            skLineSegment(sketch, "E8.55.0", {"start": v(-6.5, -16.52) * mm, "end": v(-6.14, -16.12) * mm});
            skLineSegment(sketch, "E8.55.1", {"start": v(-6.85, -16.38) * mm, "end": v(-6.83, -15.84) * mm});
            skLineSegment(sketch, "E8.55.2", {"start": v(-6.83, -15.84) * mm, "end": v(-7, -15.77) * mm});
            skLineSegment(sketch, "E8.55.3", {"start": v(-6.14, -16.12) * mm, "end": v(-5.97, -16.19) * mm});
            skLineSegment(sketch, "E8.55.4", {"start": v(-6.67, -16.45) * mm, "end": v(-6.85, -16.38) * mm});
            skLineSegment(sketch, "E8.55.5", {"start": v(-6.67, -16.45) * mm, "end": v(-6.5, -16.52) * mm});
            skLineSegment(sketch, "E8.56.0", {"start": v(-7.55, -16.07) * mm, "end": v(-7.16, -15.7) * mm});
            skLineSegment(sketch, "E8.56.1", {"start": v(-7.88, -15.9) * mm, "end": v(-7.83, -15.37) * mm});
            skLineSegment(sketch, "E8.56.2", {"start": v(-7.83, -15.37) * mm, "end": v(-8, -15.29) * mm});
            skLineSegment(sketch, "E8.56.3", {"start": v(-7.16, -15.7) * mm, "end": v(-7, -15.77) * mm});
            skLineSegment(sketch, "E8.56.4", {"start": v(-7.71, -15.99) * mm, "end": v(-7.88, -15.9) * mm});
            skLineSegment(sketch, "E8.56.5", {"start": v(-7.71, -15.99) * mm, "end": v(-7.55, -16.07) * mm});
            skLineSegment(sketch, "E8.57.0", {"start": v(-8.56, -15.55) * mm, "end": v(-8.15, -15.2) * mm});
            skLineSegment(sketch, "E8.57.1", {"start": v(-8.88, -15.37) * mm, "end": v(-8.8, -14.84) * mm});
            skLineSegment(sketch, "E8.57.2", {"start": v(-8.8, -14.84) * mm, "end": v(-8.96, -14.74) * mm});
            skLineSegment(sketch, "E8.57.3", {"start": v(-8.15, -15.2) * mm, "end": v(-7.99, -15.3) * mm});
            skLineSegment(sketch, "E8.57.4", {"start": v(-8.72, -15.46) * mm, "end": v(-8.88, -15.37) * mm});
            skLineSegment(sketch, "E8.57.5", {"start": v(-8.72, -15.46) * mm, "end": v(-8.56, -15.55) * mm});
            skLineSegment(sketch, "E8.58.0", {"start": v(-9.54, -14.97) * mm, "end": v(-9.1, -14.65) * mm});
            skLineSegment(sketch, "E8.58.1", {"start": v(-9.85, -14.77) * mm, "end": v(-9.73, -14.24) * mm});
            skLineSegment(sketch, "E8.58.2", {"start": v(-9.73, -14.24) * mm, "end": v(-9.88, -14.14) * mm});
            skLineSegment(sketch, "E8.58.3", {"start": v(-9.1, -14.65) * mm, "end": v(-8.95, -14.75) * mm});
            skLineSegment(sketch, "E8.58.4", {"start": v(-9.7, -14.87) * mm, "end": v(-9.85, -14.77) * mm});
            skLineSegment(sketch, "E8.58.5", {"start": v(-9.7, -14.87) * mm, "end": v(-9.54, -14.97) * mm});
            skLineSegment(sketch, "E8.59.0", {"start": v(-10.48, -14.33) * mm, "end": v(-10.03, -14.04) * mm});
            skLineSegment(sketch, "E8.59.1", {"start": v(-10.78, -14.1) * mm, "end": v(-10.62, -13.6) * mm});
            skLineSegment(sketch, "E8.59.2", {"start": v(-10.62, -13.6) * mm, "end": v(-10.77, -13.48) * mm});
            skLineSegment(sketch, "E8.59.3", {"start": v(-10.03, -14.04) * mm, "end": v(-9.88, -14.14) * mm});
            skLineSegment(sketch, "E8.59.4", {"start": v(-10.63, -14.22) * mm, "end": v(-10.78, -14.1) * mm});
            skLineSegment(sketch, "E8.59.5", {"start": v(-10.63, -14.22) * mm, "end": v(-10.48, -14.33) * mm});
            skLineSegment(sketch, "E8.60.0", {"start": v(-11.38, -13.63) * mm, "end": v(-10.9, -13.36) * mm});
            skLineSegment(sketch, "E8.60.1", {"start": v(-11.66, -13.39) * mm, "end": v(-11.47, -12.88) * mm});
            skLineSegment(sketch, "E8.60.2", {"start": v(-11.47, -12.88) * mm, "end": v(-11.61, -12.76) * mm});
            skLineSegment(sketch, "E8.60.3", {"start": v(-10.9, -13.36) * mm, "end": v(-10.76, -13.48) * mm});
            skLineSegment(sketch, "E8.60.4", {"start": v(-11.52, -13.5) * mm, "end": v(-11.66, -13.39) * mm});
            skLineSegment(sketch, "E8.60.5", {"start": v(-11.52, -13.5) * mm, "end": v(-11.38, -13.63) * mm});
            skLineSegment(sketch, "E8.61.0", {"start": v(-12.23, -12.87) * mm, "end": v(-11.74, -12.64) * mm});
            skLineSegment(sketch, "E8.61.1", {"start": v(-12.5, -12.61) * mm, "end": v(-12.27, -12.12) * mm});
            skLineSegment(sketch, "E8.61.2", {"start": v(-12.27, -12.12) * mm, "end": v(-12.4, -11.99) * mm});
            skLineSegment(sketch, "E8.61.3", {"start": v(-11.74, -12.64) * mm, "end": v(-11.6, -12.76) * mm});
            skLineSegment(sketch, "E8.61.4", {"start": v(-12.36, -12.74) * mm, "end": v(-12.5, -12.61) * mm});
            skLineSegment(sketch, "E8.61.5", {"start": v(-12.36, -12.74) * mm, "end": v(-12.23, -12.87) * mm});
            skLineSegment(sketch, "E8.62.0", {"start": v(-13.02, -12.06) * mm, "end": v(-12.53, -11.86) * mm});
            skLineSegment(sketch, "E8.62.1", {"start": v(-13.27, -11.78) * mm, "end": v(-13.03, -11.3) * mm});
            skLineSegment(sketch, "E8.62.2", {"start": v(-13.03, -11.3) * mm, "end": v(-13.15, -11.17) * mm});
            skLineSegment(sketch, "E8.62.3", {"start": v(-12.53, -11.86) * mm, "end": v(-12.4, -12) * mm});
            skLineSegment(sketch, "E8.62.4", {"start": v(-13.15, -11.92) * mm, "end": v(-13.27, -11.78) * mm});
            skLineSegment(sketch, "E8.62.5", {"start": v(-13.15, -11.92) * mm, "end": v(-13.02, -12.06) * mm});
            skLineSegment(sketch, "E8.63.0", {"start": v(-13.77, -11.2) * mm, "end": v(-13.26, -11.03) * mm});
            skLineSegment(sketch, "E8.63.1", {"start": v(-14, -10.9) * mm, "end": v(-13.72, -10.45) * mm});
            skLineSegment(sketch, "E8.63.2", {"start": v(-13.72, -10.45) * mm, "end": v(-13.84, -10.3) * mm});
            skLineSegment(sketch, "E8.63.3", {"start": v(-13.26, -11.03) * mm, "end": v(-13.14, -11.18) * mm});
            skLineSegment(sketch, "E8.63.4", {"start": v(-13.89, -11.06) * mm, "end": v(-14, -10.9) * mm});
            skLineSegment(sketch, "E8.63.5", {"start": v(-13.89, -11.06) * mm, "end": v(-13.77, -11.2) * mm});
            skLineSegment(sketch, "E8.64.0", {"start": v(-14.46, -10.3) * mm, "end": v(-13.94, -10.16) * mm});
            skLineSegment(sketch, "E8.64.1", {"start": v(-14.67, -10) * mm, "end": v(-14.37, -9.55) * mm});
            skLineSegment(sketch, "E8.64.2", {"start": v(-14.37, -9.55) * mm, "end": v(-14.47, -9.4) * mm});
            skLineSegment(sketch, "E8.64.3", {"start": v(-13.94, -10.16) * mm, "end": v(-13.83, -10.31) * mm});
            skLineSegment(sketch, "E8.64.4", {"start": v(-14.57, -10.14) * mm, "end": v(-14.67, -10) * mm});
            skLineSegment(sketch, "E8.64.5", {"start": v(-14.57, -10.14) * mm, "end": v(-14.46, -10.3) * mm});
            skLineSegment(sketch, "E8.65.0", {"start": v(-15.1, -9.35) * mm, "end": v(-14.56, -9.25) * mm});
            skLineSegment(sketch, "E8.65.1", {"start": v(-15.28, -9.03) * mm, "end": v(-14.95, -8.6) * mm});
            skLineSegment(sketch, "E8.65.2", {"start": v(-14.95, -8.6) * mm, "end": v(-15.04, -8.45) * mm});
            skLineSegment(sketch, "E8.65.3", {"start": v(-14.56, -9.25) * mm, "end": v(-14.46, -9.4) * mm});
            skLineSegment(sketch, "E8.65.4", {"start": v(-15.19, -9.19) * mm, "end": v(-15.28, -9.03) * mm});
            skLineSegment(sketch, "E8.65.5", {"start": v(-15.19, -9.19) * mm, "end": v(-15.1, -9.35) * mm});
            skLineSegment(sketch, "E8.66.0", {"start": v(-15.66, -8.36) * mm, "end": v(-15.13, -8.3) * mm});
            skLineSegment(sketch, "E8.66.1", {"start": v(-15.83, -8.03) * mm, "end": v(-15.47, -7.63) * mm});
            skLineSegment(sketch, "E8.66.2", {"start": v(-15.47, -7.63) * mm, "end": v(-15.55, -7.47) * mm});
            skLineSegment(sketch, "E8.66.3", {"start": v(-15.13, -8.3) * mm, "end": v(-15.04, -8.46) * mm});
            skLineSegment(sketch, "E8.66.4", {"start": v(-15.74, -8.2) * mm, "end": v(-15.83, -8.03) * mm});
            skLineSegment(sketch, "E8.66.5", {"start": v(-15.74, -8.2) * mm, "end": v(-15.66, -8.36) * mm});
            skLineSegment(sketch, "E8.67.0", {"start": v(-16.16, -7.34) * mm, "end": v(-15.63, -7.3) * mm});
            skLineSegment(sketch, "E8.67.1", {"start": v(-16.31, -7) * mm, "end": v(-15.93, -6.63) * mm});
            skLineSegment(sketch, "E8.67.2", {"start": v(-15.93, -6.63) * mm, "end": v(-16, -6.46) * mm});
            skLineSegment(sketch, "E8.67.3", {"start": v(-15.63, -7.3) * mm, "end": v(-15.55, -7.48) * mm});
            skLineSegment(sketch, "E8.67.4", {"start": v(-16.24, -7.17) * mm, "end": v(-16.31, -7) * mm});
            skLineSegment(sketch, "E8.67.5", {"start": v(-16.24, -7.17) * mm, "end": v(-16.16, -7.34) * mm});
            skLineSegment(sketch, "E8.68.0", {"start": v(-16.6, -6.29) * mm, "end": v(-16.06, -6.3) * mm});
            skLineSegment(sketch, "E8.68.1", {"start": v(-16.73, -5.94) * mm, "end": v(-16.32, -5.6) * mm});
            skLineSegment(sketch, "E8.68.2", {"start": v(-16.32, -5.6) * mm, "end": v(-16.38, -5.42) * mm});
            skLineSegment(sketch, "E8.68.3", {"start": v(-16.06, -6.3) * mm, "end": v(-16, -6.46) * mm});
            skLineSegment(sketch, "E8.68.4", {"start": v(-16.66, -6.12) * mm, "end": v(-16.73, -5.94) * mm});
            skLineSegment(sketch, "E8.68.5", {"start": v(-16.66, -6.12) * mm, "end": v(-16.6, -6.29) * mm});
            skLineSegment(sketch, "E8.69.0", {"start": v(-16.97, -5.21) * mm, "end": v(-16.43, -5.25) * mm});
            skLineSegment(sketch, "E8.69.1", {"start": v(-17.07, -4.86) * mm, "end": v(-16.64, -4.54) * mm});
            skLineSegment(sketch, "E8.69.2", {"start": v(-16.64, -4.54) * mm, "end": v(-16.7, -4.36) * mm});
            skLineSegment(sketch, "E8.69.3", {"start": v(-16.43, -5.25) * mm, "end": v(-16.38, -5.43) * mm});
            skLineSegment(sketch, "E8.69.4", {"start": v(-17.02, -5.03) * mm, "end": v(-17.07, -4.86) * mm});
            skLineSegment(sketch, "E8.69.5", {"start": v(-17.02, -5.03) * mm, "end": v(-16.97, -5.21) * mm});
            skLineSegment(sketch, "E8.70.0", {"start": v(-17.27, -4.11) * mm, "end": v(-16.73, -4.18) * mm});
            skLineSegment(sketch, "E8.70.1", {"start": v(-17.35, -3.75) * mm, "end": v(-16.9, -3.46) * mm});
            skLineSegment(sketch, "E8.70.2", {"start": v(-16.9, -3.46) * mm, "end": v(-16.94, -3.28) * mm});
            skLineSegment(sketch, "E8.70.3", {"start": v(-16.73, -4.18) * mm, "end": v(-16.7, -4.37) * mm});
            skLineSegment(sketch, "E8.70.4", {"start": v(-17.3, -3.93) * mm, "end": v(-17.35, -3.75) * mm});
            skLineSegment(sketch, "E8.70.5", {"start": v(-17.3, -3.93) * mm, "end": v(-17.27, -4.11) * mm});
            skLineSegment(sketch, "E8.71.0", {"start": v(-17.5, -3) * mm, "end": v(-16.97, -3.1) * mm});
            skLineSegment(sketch, "E8.71.1", {"start": v(-17.55, -2.63) * mm, "end": v(-17.09, -2.37) * mm});
            skLineSegment(sketch, "E8.71.2", {"start": v(-17.09, -2.37) * mm, "end": v(-17.11, -2.19) * mm});
            skLineSegment(sketch, "E8.71.3", {"start": v(-16.97, -3.1) * mm, "end": v(-16.94, -3.29) * mm});
            skLineSegment(sketch, "E8.71.4", {"start": v(-17.53, -2.82) * mm, "end": v(-17.55, -2.63) * mm});
            skLineSegment(sketch, "E8.71.5", {"start": v(-17.53, -2.82) * mm, "end": v(-17.5, -3) * mm});
            skLineSegment(sketch, "E8.72.0", {"start": v(-17.65, -1.87) * mm, "end": v(-17.13, -2) * mm});
            skLineSegment(sketch, "E8.72.1", {"start": v(-17.69, -1.5) * mm, "end": v(-17.2, -1.27) * mm});
            skLineSegment(sketch, "E8.72.2", {"start": v(-17.2, -1.27) * mm, "end": v(-17.22, -1.08) * mm});
            skLineSegment(sketch, "E8.72.3", {"start": v(-17.13, -2) * mm, "end": v(-17.11, -2.2) * mm});
            skLineSegment(sketch, "E8.72.4", {"start": v(-17.67, -1.69) * mm, "end": v(-17.69, -1.5) * mm});
            skLineSegment(sketch, "E8.72.5", {"start": v(-17.67, -1.69) * mm, "end": v(-17.65, -1.87) * mm});
            skLineSegment(sketch, "E8.73.0", {"start": v(-17.74, -0.74) * mm, "end": v(-17.23, -0.9) * mm});
            skLineSegment(sketch, "E8.73.1", {"start": v(-17.75, -0.37) * mm, "end": v(-17.25, -0.16) * mm});
            skLineSegment(sketch, "E8.73.2", {"start": v(-17.25, -0.16) * mm, "end": v(-17.25, 0.02) * mm});
            skLineSegment(sketch, "E8.73.3", {"start": v(-17.23, -0.9) * mm, "end": v(-17.22, -1.1) * mm});
            skLineSegment(sketch, "E8.73.4", {"start": v(-17.74, -0.55) * mm, "end": v(-17.75, -0.37) * mm});
            skLineSegment(sketch, "E8.73.5", {"start": v(-17.74, -0.55) * mm, "end": v(-17.74, -0.74) * mm});
            skLineSegment(sketch, "E8.74.0", {"start": v(-17.75, 0.4) * mm, "end": v(-17.25, 0.2) * mm});
            skLineSegment(sketch, "E8.74.1", {"start": v(-17.73, 0.77) * mm, "end": v(-17.22, 0.94) * mm});
            skLineSegment(sketch, "E8.74.2", {"start": v(-17.22, 0.94) * mm, "end": v(-17.21, 1.13) * mm});
            skLineSegment(sketch, "E8.74.3", {"start": v(-17.25, 0.2) * mm, "end": v(-17.25, 0.01) * mm});
            skLineSegment(sketch, "E8.74.4", {"start": v(-17.74, 0.59) * mm, "end": v(-17.73, 0.77) * mm});
            skLineSegment(sketch, "E8.74.5", {"start": v(-17.74, 0.59) * mm, "end": v(-17.75, 0.4) * mm});
            skLineSegment(sketch, "E8.75.0", {"start": v(-17.68, 1.54) * mm, "end": v(-17.2, 1.3) * mm});
            skLineSegment(sketch, "E8.75.1", {"start": v(-17.65, 1.9) * mm, "end": v(-17.13, 2.04) * mm});
            skLineSegment(sketch, "E8.75.2", {"start": v(-17.13, 2.04) * mm, "end": v(-17.1, 2.23) * mm});
            skLineSegment(sketch, "E8.75.3", {"start": v(-17.2, 1.3) * mm, "end": v(-17.22, 1.12) * mm});
            skLineSegment(sketch, "E8.75.4", {"start": v(-17.67, 1.72) * mm, "end": v(-17.65, 1.9) * mm});
            skLineSegment(sketch, "E8.75.5", {"start": v(-17.67, 1.72) * mm, "end": v(-17.68, 1.54) * mm});
            skLineSegment(sketch, "E8.76.0", {"start": v(-17.55, 2.67) * mm, "end": v(-17.08, 2.4) * mm});
            skLineSegment(sketch, "E8.76.1", {"start": v(-17.49, 3.03) * mm, "end": v(-16.96, 3.14) * mm});
            skLineSegment(sketch, "E8.76.2", {"start": v(-16.96, 3.14) * mm, "end": v(-16.93, 3.32) * mm});
            skLineSegment(sketch, "E8.76.3", {"start": v(-17.08, 2.4) * mm, "end": v(-17.1, 2.22) * mm});
            skLineSegment(sketch, "E8.76.4", {"start": v(-17.52, 2.85) * mm, "end": v(-17.49, 3.03) * mm});
            skLineSegment(sketch, "E8.76.5", {"start": v(-17.52, 2.85) * mm, "end": v(-17.55, 2.67) * mm});
            skLineSegment(sketch, "E8.77.0", {"start": v(-17.34, 3.79) * mm, "end": v(-16.9, 3.5) * mm});
            skLineSegment(sketch, "E8.77.1", {"start": v(-17.26, 4.15) * mm, "end": v(-16.73, 4.22) * mm});
            skLineSegment(sketch, "E8.77.2", {"start": v(-16.73, 4.22) * mm, "end": v(-16.68, 4.4) * mm});
            skLineSegment(sketch, "E8.77.3", {"start": v(-16.9, 3.5) * mm, "end": v(-16.93, 3.31) * mm});
            skLineSegment(sketch, "E8.77.4", {"start": v(-17.3, 3.97) * mm, "end": v(-17.26, 4.15) * mm});
            skLineSegment(sketch, "E8.77.5", {"start": v(-17.3, 3.97) * mm, "end": v(-17.34, 3.79) * mm});
            skLineSegment(sketch, "E8.78.0", {"start": v(-17.06, 4.89) * mm, "end": v(-16.63, 4.57) * mm});
            skLineSegment(sketch, "E8.78.1", {"start": v(-16.96, 5.25) * mm, "end": v(-16.42, 5.28) * mm});
            skLineSegment(sketch, "E8.78.2", {"start": v(-16.42, 5.28) * mm, "end": v(-16.37, 5.46) * mm});
            skLineSegment(sketch, "E8.78.3", {"start": v(-16.63, 4.57) * mm, "end": v(-16.68, 4.39) * mm});
            skLineSegment(sketch, "E8.78.4", {"start": v(-17.01, 5.07) * mm, "end": v(-16.96, 5.25) * mm});
            skLineSegment(sketch, "E8.78.5", {"start": v(-17.01, 5.07) * mm, "end": v(-17.06, 4.89) * mm});
            skLineSegment(sketch, "E8.79.0", {"start": v(-16.72, 5.97) * mm, "end": v(-16.3, 5.62) * mm});
            skLineSegment(sketch, "E8.79.1", {"start": v(-16.59, 6.32) * mm, "end": v(-16.05, 6.32) * mm});
            skLineSegment(sketch, "E8.79.2", {"start": v(-16.05, 6.32) * mm, "end": v(-15.98, 6.5) * mm});
            skLineSegment(sketch, "E8.79.3", {"start": v(-16.3, 5.62) * mm, "end": v(-16.37, 5.45) * mm});
            skLineSegment(sketch, "E8.79.4", {"start": v(-16.65, 6.15) * mm, "end": v(-16.59, 6.32) * mm});
            skLineSegment(sketch, "E8.79.5", {"start": v(-16.65, 6.15) * mm, "end": v(-16.72, 5.97) * mm});
            skLineSegment(sketch, "E8.80.0", {"start": v(-16.3, 7.03) * mm, "end": v(-15.91, 6.66) * mm});
            skLineSegment(sketch, "E8.80.1", {"start": v(-16.15, 7.37) * mm, "end": v(-15.61, 7.34) * mm});
            skLineSegment(sketch, "E8.80.2", {"start": v(-15.61, 7.34) * mm, "end": v(-15.53, 7.5) * mm});
            skLineSegment(sketch, "E8.80.3", {"start": v(-15.91, 6.66) * mm, "end": v(-15.99, 6.49) * mm});
            skLineSegment(sketch, "E8.80.4", {"start": v(-16.22, 7.2) * mm, "end": v(-16.15, 7.37) * mm});
            skLineSegment(sketch, "E8.80.5", {"start": v(-16.22, 7.2) * mm, "end": v(-16.3, 7.03) * mm});
            skLineSegment(sketch, "E8.81.0", {"start": v(-15.81, 8.06) * mm, "end": v(-15.45, 7.66) * mm});
            skLineSegment(sketch, "E8.81.1", {"start": v(-15.64, 8.4) * mm, "end": v(-15.1, 8.32) * mm});
            skLineSegment(sketch, "E8.81.2", {"start": v(-15.1, 8.32) * mm, "end": v(-15.02, 8.49) * mm});
            skLineSegment(sketch, "E8.81.3", {"start": v(-15.45, 7.66) * mm, "end": v(-15.54, 7.5) * mm});
            skLineSegment(sketch, "E8.81.4", {"start": v(-15.73, 8.23) * mm, "end": v(-15.64, 8.4) * mm});
            skLineSegment(sketch, "E8.81.5", {"start": v(-15.73, 8.23) * mm, "end": v(-15.81, 8.06) * mm});
            skLineSegment(sketch, "E8.82.0", {"start": v(-15.27, 9.06) * mm, "end": v(-14.93, 8.64) * mm});
            skLineSegment(sketch, "E8.82.1", {"start": v(-15.07, 9.38) * mm, "end": v(-14.54, 9.27) * mm});
            skLineSegment(sketch, "E8.82.2", {"start": v(-14.54, 9.27) * mm, "end": v(-14.45, 9.43) * mm});
            skLineSegment(sketch, "E8.82.3", {"start": v(-14.93, 8.64) * mm, "end": v(-15.02, 8.48) * mm});
            skLineSegment(sketch, "E8.82.4", {"start": v(-15.17, 9.22) * mm, "end": v(-15.07, 9.38) * mm});
            skLineSegment(sketch, "E8.82.5", {"start": v(-15.17, 9.22) * mm, "end": v(-15.27, 9.06) * mm});
            skLineSegment(sketch, "E8.83.0", {"start": v(-14.65, 10.02) * mm, "end": v(-14.35, 9.58) * mm});
            skLineSegment(sketch, "E8.83.1", {"start": v(-14.44, 10.32) * mm, "end": v(-13.92, 10.19) * mm});
            skLineSegment(sketch, "E8.83.2", {"start": v(-13.92, 10.19) * mm, "end": v(-13.81, 10.34) * mm});
            skLineSegment(sketch, "E8.83.3", {"start": v(-14.35, 9.58) * mm, "end": v(-14.45, 9.42) * mm});
            skLineSegment(sketch, "E8.83.4", {"start": v(-14.55, 10.17) * mm, "end": v(-14.44, 10.32) * mm});
            skLineSegment(sketch, "E8.83.5", {"start": v(-14.55, 10.17) * mm, "end": v(-14.65, 10.02) * mm});
            skLineSegment(sketch, "E8.84.0", {"start": v(-13.98, 10.94) * mm, "end": v(-13.7, 10.48) * mm});
            skLineSegment(sketch, "E8.84.1", {"start": v(-13.75, 11.23) * mm, "end": v(-13.24, 11.06) * mm});
            skLineSegment(sketch, "E8.84.2", {"start": v(-13.24, 11.06) * mm, "end": v(-13.12, 11.2) * mm});
            skLineSegment(sketch, "E8.84.3", {"start": v(-13.7, 10.48) * mm, "end": v(-13.82, 10.33) * mm});
            skLineSegment(sketch, "E8.84.4", {"start": v(-13.87, 11.08) * mm, "end": v(-13.75, 11.23) * mm});
            skLineSegment(sketch, "E8.84.5", {"start": v(-13.87, 11.08) * mm, "end": v(-13.98, 10.94) * mm});
            skLineSegment(sketch, "E8.85.0", {"start": v(-13.25, 11.81) * mm, "end": v(-13, 11.33) * mm});
            skLineSegment(sketch, "E8.85.1", {"start": v(-13, 12.09) * mm, "end": v(-12.5, 11.88) * mm});
            skLineSegment(sketch, "E8.85.2", {"start": v(-12.5, 11.88) * mm, "end": v(-12.38, 12.02) * mm});
            skLineSegment(sketch, "E8.85.3", {"start": v(-13, 11.33) * mm, "end": v(-13.13, 11.2) * mm});
            skLineSegment(sketch, "E8.85.4", {"start": v(-13.13, 11.95) * mm, "end": v(-13, 12.09) * mm});
            skLineSegment(sketch, "E8.85.5", {"start": v(-13.13, 11.95) * mm, "end": v(-13.25, 11.81) * mm});
            skLineSegment(sketch, "E8.86.0", {"start": v(-12.47, 12.64) * mm, "end": v(-12.25, 12.14) * mm});
            skLineSegment(sketch, "E8.86.1", {"start": v(-12.2, 12.9) * mm, "end": v(-11.72, 12.66) * mm});
            skLineSegment(sketch, "E8.86.2", {"start": v(-11.72, 12.66) * mm, "end": v(-11.58, 12.79) * mm});
            skLineSegment(sketch, "E8.86.3", {"start": v(-12.25, 12.14) * mm, "end": v(-12.38, 12.01) * mm});
            skLineSegment(sketch, "E8.86.4", {"start": v(-12.33, 12.76) * mm, "end": v(-12.2, 12.9) * mm});
            skLineSegment(sketch, "E8.86.5", {"start": v(-12.33, 12.76) * mm, "end": v(-12.47, 12.64) * mm});
            skLineSegment(sketch, "E8.87.0", {"start": v(-11.63, 13.4) * mm, "end": v(-11.45, 12.9) * mm});
            skLineSegment(sketch, "E8.87.1", {"start": v(-11.35, 13.65) * mm, "end": v(-10.88, 13.39) * mm});
            skLineSegment(sketch, "E8.87.2", {"start": v(-10.88, 13.39) * mm, "end": v(-10.74, 13.5) * mm});
            skLineSegment(sketch, "E8.87.3", {"start": v(-11.45, 12.9) * mm, "end": v(-11.59, 12.78) * mm});
            skLineSegment(sketch, "E8.87.4", {"start": v(-11.5, 13.53) * mm, "end": v(-11.35, 13.65) * mm});
            skLineSegment(sketch, "E8.87.5", {"start": v(-11.5, 13.53) * mm, "end": v(-11.63, 13.4) * mm});
            skLineSegment(sketch, "E8.88.0", {"start": v(-10.75, 14.13) * mm, "end": v(-10.6, 13.61) * mm});
            skLineSegment(sketch, "E8.88.1", {"start": v(-10.45, 14.35) * mm, "end": v(-10, 14.06) * mm});
            skLineSegment(sketch, "E8.88.2", {"start": v(-10, 14.06) * mm, "end": v(-9.85, 14.16) * mm});
            skLineSegment(sketch, "E8.88.3", {"start": v(-10.6, 13.61) * mm, "end": v(-10.74, 13.5) * mm});
            skLineSegment(sketch, "E8.88.4", {"start": v(-10.6, 14.24) * mm, "end": v(-10.45, 14.35) * mm});
            skLineSegment(sketch, "E8.88.5", {"start": v(-10.6, 14.24) * mm, "end": v(-10.75, 14.13) * mm});
            skLineSegment(sketch, "E8.89.0", {"start": v(-9.82, 14.79) * mm, "end": v(-9.7, 14.26) * mm});
            skLineSegment(sketch, "E8.89.1", {"start": v(-9.5, 14.99) * mm, "end": v(-9.08, 14.67) * mm});
            skLineSegment(sketch, "E8.89.2", {"start": v(-9.08, 14.67) * mm, "end": v(-8.92, 14.77) * mm});
            skLineSegment(sketch, "E8.89.3", {"start": v(-9.7, 14.26) * mm, "end": v(-9.86, 14.16) * mm});
            skLineSegment(sketch, "E8.89.4", {"start": v(-9.67, 14.89) * mm, "end": v(-9.5, 14.99) * mm});
            skLineSegment(sketch, "E8.89.5", {"start": v(-9.67, 14.89) * mm, "end": v(-9.82, 14.79) * mm});
            skLineSegment(sketch, "E8.90.0", {"start": v(-8.85, 15.39) * mm, "end": v(-8.77, 14.85) * mm});
            skLineSegment(sketch, "E8.90.1", {"start": v(-8.53, 15.57) * mm, "end": v(-8.12, 15.22) * mm});
            skLineSegment(sketch, "E8.90.2", {"start": v(-8.12, 15.22) * mm, "end": v(-7.96, 15.3) * mm});
            skLineSegment(sketch, "E8.90.3", {"start": v(-8.77, 14.85) * mm, "end": v(-8.93, 14.76) * mm});
            skLineSegment(sketch, "E8.90.4", {"start": v(-8.7, 15.48) * mm, "end": v(-8.53, 15.57) * mm});
            skLineSegment(sketch, "E8.90.5", {"start": v(-8.7, 15.48) * mm, "end": v(-8.85, 15.39) * mm});
            skLineSegment(sketch, "E8.91.0", {"start": v(-7.85, 15.92) * mm, "end": v(-7.8, 15.39) * mm});
            skLineSegment(sketch, "E8.91.1", {"start": v(-7.51, 16.08) * mm, "end": v(-7.13, 15.7) * mm});
            skLineSegment(sketch, "E8.91.2", {"start": v(-7.13, 15.7) * mm, "end": v(-6.96, 15.79) * mm});
            skLineSegment(sketch, "E8.91.3", {"start": v(-7.8, 15.39) * mm, "end": v(-7.97, 15.3) * mm});
            skLineSegment(sketch, "E8.91.4", {"start": v(-7.68, 16) * mm, "end": v(-7.51, 16.08) * mm});
            skLineSegment(sketch, "E8.91.5", {"start": v(-7.68, 16) * mm, "end": v(-7.85, 15.92) * mm});
            skLineSegment(sketch, "E8.92.0", {"start": v(-6.81, 16.4) * mm, "end": v(-6.8, 15.85) * mm});
            skLineSegment(sketch, "E8.92.1", {"start": v(-6.47, 16.53) * mm, "end": v(-6.1, 16.13) * mm});
            skLineSegment(sketch, "E8.92.2", {"start": v(-6.1, 16.13) * mm, "end": v(-5.93, 16.2) * mm});
            skLineSegment(sketch, "E8.92.3", {"start": v(-6.8, 15.85) * mm, "end": v(-6.97, 15.78) * mm});
            skLineSegment(sketch, "E8.92.4", {"start": v(-6.64, 16.46) * mm, "end": v(-6.47, 16.53) * mm});
            skLineSegment(sketch, "E8.92.5", {"start": v(-6.64, 16.46) * mm, "end": v(-6.81, 16.4) * mm});
            skLineSegment(sketch, "E8.93.0", {"start": v(-5.75, 16.8) * mm, "end": v(-5.77, 16.26) * mm});
            skLineSegment(sketch, "E8.93.1", {"start": v(-5.4, 16.91) * mm, "end": v(-5.06, 16.5) * mm});
            skLineSegment(sketch, "E8.93.2", {"start": v(-5.06, 16.5) * mm, "end": v(-4.88, 16.55) * mm});
            skLineSegment(sketch, "E8.93.3", {"start": v(-5.77, 16.26) * mm, "end": v(-5.94, 16.2) * mm});
            skLineSegment(sketch, "E8.93.4", {"start": v(-5.57, 16.85) * mm, "end": v(-5.4, 16.91) * mm});
            skLineSegment(sketch, "E8.93.5", {"start": v(-5.57, 16.85) * mm, "end": v(-5.75, 16.8) * mm});
            skLineSegment(sketch, "E8.94.0", {"start": v(-4.66, 17.13) * mm, "end": v(-4.71, 16.6) * mm});
            skLineSegment(sketch, "E8.94.1", {"start": v(-4.3, 17.22) * mm, "end": v(-4, 16.78) * mm});
            skLineSegment(sketch, "E8.94.2", {"start": v(-4, 16.78) * mm, "end": v(-3.81, 16.82) * mm});
            skLineSegment(sketch, "E8.94.3", {"start": v(-4.71, 16.6) * mm, "end": v(-4.9, 16.54) * mm});
            skLineSegment(sketch, "E8.94.4", {"start": v(-4.48, 17.18) * mm, "end": v(-4.3, 17.22) * mm});
            skLineSegment(sketch, "E8.94.5", {"start": v(-4.48, 17.18) * mm, "end": v(-4.66, 17.13) * mm});
            skLineSegment(sketch, "E8.95.0", {"start": v(-3.55, 17.4) * mm, "end": v(-3.64, 16.86) * mm});
            skLineSegment(sketch, "E8.95.1", {"start": v(-3.19, 17.46) * mm, "end": v(-2.91, 17) * mm});
            skLineSegment(sketch, "E8.95.2", {"start": v(-2.91, 17) * mm, "end": v(-2.73, 17.03) * mm});
            skLineSegment(sketch, "E8.95.3", {"start": v(-3.64, 16.86) * mm, "end": v(-3.82, 16.82) * mm});
            skLineSegment(sketch, "E8.95.4", {"start": v(-3.37, 17.43) * mm, "end": v(-3.19, 17.46) * mm});
            skLineSegment(sketch, "E8.95.5", {"start": v(-3.37, 17.43) * mm, "end": v(-3.55, 17.4) * mm});
            skLineSegment(sketch, "E8.96.0", {"start": v(-2.43, 17.58) * mm, "end": v(-2.55, 17.06) * mm});
            skLineSegment(sketch, "E8.96.1", {"start": v(-2.06, 17.63) * mm, "end": v(-1.81, 17.15) * mm});
            skLineSegment(sketch, "E8.96.2", {"start": v(-1.81, 17.15) * mm, "end": v(-1.63, 17.17) * mm});
            skLineSegment(sketch, "E8.96.3", {"start": v(-2.55, 17.06) * mm, "end": v(-2.74, 17.03) * mm});
            skLineSegment(sketch, "E8.96.4", {"start": v(-2.25, 17.6) * mm, "end": v(-2.06, 17.63) * mm});
            skLineSegment(sketch, "E8.96.5", {"start": v(-2.25, 17.6) * mm, "end": v(-2.43, 17.58) * mm});
            skLineSegment(sketch, "E8.97.0", {"start": v(-1.3, 17.7) * mm, "end": v(-1.45, 17.19) * mm});
            skLineSegment(sketch, "E8.97.1", {"start": v(-0.93, 17.73) * mm, "end": v(-0.71, 17.24) * mm});
            skLineSegment(sketch, "E8.97.2", {"start": v(-0.71, 17.24) * mm, "end": v(-0.53, 17.24) * mm});
            skLineSegment(sketch, "E8.97.3", {"start": v(-1.45, 17.19) * mm, "end": v(-1.64, 17.17) * mm});
            skLineSegment(sketch, "E8.97.4", {"start": v(-1.11, 17.71) * mm, "end": v(-0.93, 17.73) * mm});
            skLineSegment(sketch, "E8.97.5", {"start": v(-1.11, 17.71) * mm, "end": v(-1.3, 17.7) * mm});
            skPoint(sketch, "E8.center", {"position": v(0, 0) * mm});
            skLineSegment(sketch, "E8.anchor1", {"start": v(0, 0) * mm, "end": v(-0.56, 17.24) * mm, "construction": true});
            skLineSegment(sketch, "E8.anchor2", {"start": v(0, 0) * mm, "end": v(-1.64, 17.17) * mm, "construction": true});
            skSolve(sketch);
        }
        {
            var Q0;
            Q0 = qSketchRegion(id + "F0", true);
            extrude(context, id + "F1", {"entities" : qUnion([Q0]), "depth" : .5 * mm, "offsetDistance" : 25 * mm});
        }
        {
            var Q0;
            Q0=makeQuery(id+"F0.imprint","IMPRINT",FACE,{"disambiguationData":[TD([[makeQuery(id+"F0.imprint","IMPRINT",EDGE,{"derivedFrom":sQuery(id+"F0.wireOp",EDGE,"E2")}),1.0]])]});
            var sketch = newSketch(context, id + "F2", { "sketchPlane" : qUnion([Q0])});
            skCircle(sketch, "E9", {"center": v(0, 0) * mm, "radius": 4.9 * mm});
            skSolve(sketch);
        }
        {
            var Q0;
            Q0 = qSketchRegion(id + "F2", true);
            extrude(context, id + "F3", {"entities" : qUnion([Q0]), "oppositeDirection" : true, "depth" : 10 * mm, "offsetDistance" : 25 * mm});
        }
        {
            var Q0;
            Q0=makeQuery(id+"F1.opExtrude","CAP_FACE",FACE,{"disambiguationData":[OSD([sQuery(id+"F0.wireOp",EDGE,"E2"),sQuery(id+"F0.wireOp",EDGE,"E3"),sQuery(id+"F0.wireOp",EDGE,"E4"),sQuery(id+"F0.wireOp",EDGE,"E5.MirrorCS"),sQuery(id+"F0.wireOp",EDGE,"E6.MirrorCS"),sQuery(id+"F0.wireOp",EDGE,"E7.MirrorCS"),sQuery(id+"F0.wireOp",EDGE,"E8.1.0"),sQuery(id+"F0.wireOp",EDGE,"E8.1.1"),sQuery(id+"F0.wireOp",EDGE,"E8.1.2"),sQuery(id+"F0.wireOp",EDGE,"E8.1.3"),sQuery(id+"F0.wireOp",EDGE,"E8.1.4"),sQuery(id+"F0.wireOp",EDGE,"E8.1.5"),sQuery(id+"F0.wireOp",EDGE,"E8.2.0"),sQuery(id+"F0.wireOp",EDGE,"E8.2.1"),sQuery(id+"F0.wireOp",EDGE,"E8.2.2"),sQuery(id+"F0.wireOp",EDGE,"E8.2.3"),sQuery(id+"F0.wireOp",EDGE,"E8.2.4"),sQuery(id+"F0.wireOp",EDGE,"E8.2.5"),sQuery(id+"F0.wireOp",EDGE,"E8.3.0"),sQuery(id+"F0.wireOp",EDGE,"E8.3.1"),sQuery(id+"F0.wireOp",EDGE,"E8.3.2"),sQuery(id+"F0.wireOp",EDGE,"E8.3.3"),sQuery(id+"F0.wireOp",EDGE,"E8.3.4"),sQuery(id+"F0.wireOp",EDGE,"E8.3.5"),sQuery(id+"F0.wireOp",EDGE,"E8.4.0"),sQuery(id+"F0.wireOp",EDGE,"E8.4.1"),sQuery(id+"F0.wireOp",EDGE,"E8.4.2"),sQuery(id+"F0.wireOp",EDGE,"E8.4.3"),sQuery(id+"F0.wireOp",EDGE,"E8.4.4"),sQuery(id+"F0.wireOp",EDGE,"E8.4.5"),sQuery(id+"F0.wireOp",EDGE,"E8.5.0"),sQuery(id+"F0.wireOp",EDGE,"E8.5.1"),sQuery(id+"F0.wireOp",EDGE,"E8.5.2"),sQuery(id+"F0.wireOp",EDGE,"E8.5.3"),sQuery(id+"F0.wireOp",EDGE,"E8.5.4"),sQuery(id+"F0.wireOp",EDGE,"E8.5.5"),sQuery(id+"F0.wireOp",EDGE,"E8.6.0"),sQuery(id+"F0.wireOp",EDGE,"E8.6.1"),sQuery(id+"F0.wireOp",EDGE,"E8.6.2"),sQuery(id+"F0.wireOp",EDGE,"E8.6.3"),sQuery(id+"F0.wireOp",EDGE,"E8.6.4"),sQuery(id+"F0.wireOp",EDGE,"E8.6.5"),sQuery(id+"F0.wireOp",EDGE,"E8.7.0"),sQuery(id+"F0.wireOp",EDGE,"E8.7.1"),sQuery(id+"F0.wireOp",EDGE,"E8.7.2"),sQuery(id+"F0.wireOp",EDGE,"E8.7.3"),sQuery(id+"F0.wireOp",EDGE,"E8.7.4"),sQuery(id+"F0.wireOp",EDGE,"E8.7.5"),sQuery(id+"F0.wireOp",EDGE,"E8.8.0"),sQuery(id+"F0.wireOp",EDGE,"E8.8.1"),sQuery(id+"F0.wireOp",EDGE,"E8.8.2"),sQuery(id+"F0.wireOp",EDGE,"E8.8.3"),sQuery(id+"F0.wireOp",EDGE,"E8.8.4"),sQuery(id+"F0.wireOp",EDGE,"E8.8.5"),sQuery(id+"F0.wireOp",EDGE,"E8.9.0"),sQuery(id+"F0.wireOp",EDGE,"E8.9.1"),sQuery(id+"F0.wireOp",EDGE,"E8.9.2"),sQuery(id+"F0.wireOp",EDGE,"E8.9.3"),sQuery(id+"F0.wireOp",EDGE,"E8.9.4"),sQuery(id+"F0.wireOp",EDGE,"E8.9.5"),sQuery(id+"F0.wireOp",EDGE,"E8.10.0"),sQuery(id+"F0.wireOp",EDGE,"E8.10.1"),sQuery(id+"F0.wireOp",EDGE,"E8.10.2"),sQuery(id+"F0.wireOp",EDGE,"E8.10.3"),sQuery(id+"F0.wireOp",EDGE,"E8.10.4"),sQuery(id+"F0.wireOp",EDGE,"E8.10.5"),sQuery(id+"F0.wireOp",EDGE,"E8.11.0"),sQuery(id+"F0.wireOp",EDGE,"E8.11.1"),sQuery(id+"F0.wireOp",EDGE,"E8.11.2"),sQuery(id+"F0.wireOp",EDGE,"E8.11.3"),sQuery(id+"F0.wireOp",EDGE,"E8.11.4"),sQuery(id+"F0.wireOp",EDGE,"E8.11.5"),sQuery(id+"F0.wireOp",EDGE,"E8.12.0"),sQuery(id+"F0.wireOp",EDGE,"E8.12.1"),sQuery(id+"F0.wireOp",EDGE,"E8.12.2"),sQuery(id+"F0.wireOp",EDGE,"E8.12.3"),sQuery(id+"F0.wireOp",EDGE,"E8.12.4"),sQuery(id+"F0.wireOp",EDGE,"E8.12.5"),sQuery(id+"F0.wireOp",EDGE,"E8.13.0"),sQuery(id+"F0.wireOp",EDGE,"E8.13.1"),sQuery(id+"F0.wireOp",EDGE,"E8.13.2"),sQuery(id+"F0.wireOp",EDGE,"E8.13.3"),sQuery(id+"F0.wireOp",EDGE,"E8.13.4"),sQuery(id+"F0.wireOp",EDGE,"E8.13.5"),sQuery(id+"F0.wireOp",EDGE,"E8.14.0"),sQuery(id+"F0.wireOp",EDGE,"E8.14.1"),sQuery(id+"F0.wireOp",EDGE,"E8.14.2"),sQuery(id+"F0.wireOp",EDGE,"E8.14.3"),sQuery(id+"F0.wireOp",EDGE,"E8.14.4"),sQuery(id+"F0.wireOp",EDGE,"E8.14.5"),sQuery(id+"F0.wireOp",EDGE,"E8.15.0"),sQuery(id+"F0.wireOp",EDGE,"E8.15.1"),sQuery(id+"F0.wireOp",EDGE,"E8.15.2"),sQuery(id+"F0.wireOp",EDGE,"E8.15.3"),sQuery(id+"F0.wireOp",EDGE,"E8.15.4"),sQuery(id+"F0.wireOp",EDGE,"E8.15.5"),sQuery(id+"F0.wireOp",EDGE,"E8.16.0"),sQuery(id+"F0.wireOp",EDGE,"E8.16.1"),sQuery(id+"F0.wireOp",EDGE,"E8.16.2"),sQuery(id+"F0.wireOp",EDGE,"E8.16.3"),sQuery(id+"F0.wireOp",EDGE,"E8.16.4"),sQuery(id+"F0.wireOp",EDGE,"E8.16.5"),sQuery(id+"F0.wireOp",EDGE,"E8.17.0"),sQuery(id+"F0.wireOp",EDGE,"E8.17.1"),sQuery(id+"F0.wireOp",EDGE,"E8.17.2"),sQuery(id+"F0.wireOp",EDGE,"E8.17.3"),sQuery(id+"F0.wireOp",EDGE,"E8.17.4"),sQuery(id+"F0.wireOp",EDGE,"E8.17.5"),sQuery(id+"F0.wireOp",EDGE,"E8.18.0"),sQuery(id+"F0.wireOp",EDGE,"E8.18.1"),sQuery(id+"F0.wireOp",EDGE,"E8.18.2"),sQuery(id+"F0.wireOp",EDGE,"E8.18.3"),sQuery(id+"F0.wireOp",EDGE,"E8.18.4"),sQuery(id+"F0.wireOp",EDGE,"E8.18.5"),sQuery(id+"F0.wireOp",EDGE,"E8.19.0"),sQuery(id+"F0.wireOp",EDGE,"E8.19.1"),sQuery(id+"F0.wireOp",EDGE,"E8.19.2"),sQuery(id+"F0.wireOp",EDGE,"E8.19.3"),sQuery(id+"F0.wireOp",EDGE,"E8.19.4"),sQuery(id+"F0.wireOp",EDGE,"E8.19.5"),sQuery(id+"F0.wireOp",EDGE,"E8.20.0"),sQuery(id+"F0.wireOp",EDGE,"E8.20.1"),sQuery(id+"F0.wireOp",EDGE,"E8.20.2"),sQuery(id+"F0.wireOp",EDGE,"E8.20.3"),sQuery(id+"F0.wireOp",EDGE,"E8.20.4"),sQuery(id+"F0.wireOp",EDGE,"E8.20.5"),sQuery(id+"F0.wireOp",EDGE,"E8.21.0"),sQuery(id+"F0.wireOp",EDGE,"E8.21.1"),sQuery(id+"F0.wireOp",EDGE,"E8.21.2"),sQuery(id+"F0.wireOp",EDGE,"E8.21.3"),sQuery(id+"F0.wireOp",EDGE,"E8.21.4"),sQuery(id+"F0.wireOp",EDGE,"E8.21.5"),sQuery(id+"F0.wireOp",EDGE,"E8.22.0"),sQuery(id+"F0.wireOp",EDGE,"E8.22.1"),sQuery(id+"F0.wireOp",EDGE,"E8.22.2"),sQuery(id+"F0.wireOp",EDGE,"E8.22.3"),sQuery(id+"F0.wireOp",EDGE,"E8.22.4"),sQuery(id+"F0.wireOp",EDGE,"E8.22.5"),sQuery(id+"F0.wireOp",EDGE,"E8.23.0"),sQuery(id+"F0.wireOp",EDGE,"E8.23.1"),sQuery(id+"F0.wireOp",EDGE,"E8.23.2"),sQuery(id+"F0.wireOp",EDGE,"E8.23.3"),sQuery(id+"F0.wireOp",EDGE,"E8.23.4"),sQuery(id+"F0.wireOp",EDGE,"E8.23.5"),sQuery(id+"F0.wireOp",EDGE,"E8.24.0"),sQuery(id+"F0.wireOp",EDGE,"E8.24.1"),sQuery(id+"F0.wireOp",EDGE,"E8.24.2"),sQuery(id+"F0.wireOp",EDGE,"E8.24.3"),sQuery(id+"F0.wireOp",EDGE,"E8.24.4"),sQuery(id+"F0.wireOp",EDGE,"E8.24.5"),sQuery(id+"F0.wireOp",EDGE,"E8.25.0"),sQuery(id+"F0.wireOp",EDGE,"E8.25.1"),sQuery(id+"F0.wireOp",EDGE,"E8.25.2"),sQuery(id+"F0.wireOp",EDGE,"E8.25.3"),sQuery(id+"F0.wireOp",EDGE,"E8.25.4"),sQuery(id+"F0.wireOp",EDGE,"E8.25.5"),sQuery(id+"F0.wireOp",EDGE,"E8.26.0"),sQuery(id+"F0.wireOp",EDGE,"E8.26.1"),sQuery(id+"F0.wireOp",EDGE,"E8.26.2"),sQuery(id+"F0.wireOp",EDGE,"E8.26.3"),sQuery(id+"F0.wireOp",EDGE,"E8.26.4"),sQuery(id+"F0.wireOp",EDGE,"E8.26.5"),sQuery(id+"F0.wireOp",EDGE,"E8.27.0"),sQuery(id+"F0.wireOp",EDGE,"E8.27.1"),sQuery(id+"F0.wireOp",EDGE,"E8.27.2"),sQuery(id+"F0.wireOp",EDGE,"E8.27.3"),sQuery(id+"F0.wireOp",EDGE,"E8.27.4"),sQuery(id+"F0.wireOp",EDGE,"E8.27.5"),sQuery(id+"F0.wireOp",EDGE,"E8.28.0"),sQuery(id+"F0.wireOp",EDGE,"E8.28.1"),sQuery(id+"F0.wireOp",EDGE,"E8.28.2"),sQuery(id+"F0.wireOp",EDGE,"E8.28.3"),sQuery(id+"F0.wireOp",EDGE,"E8.28.4"),sQuery(id+"F0.wireOp",EDGE,"E8.28.5"),sQuery(id+"F0.wireOp",EDGE,"E8.29.0"),sQuery(id+"F0.wireOp",EDGE,"E8.29.1"),sQuery(id+"F0.wireOp",EDGE,"E8.29.2"),sQuery(id+"F0.wireOp",EDGE,"E8.29.3"),sQuery(id+"F0.wireOp",EDGE,"E8.29.4"),sQuery(id+"F0.wireOp",EDGE,"E8.29.5"),sQuery(id+"F0.wireOp",EDGE,"E8.30.0"),sQuery(id+"F0.wireOp",EDGE,"E8.30.1"),sQuery(id+"F0.wireOp",EDGE,"E8.30.2"),sQuery(id+"F0.wireOp",EDGE,"E8.30.3"),sQuery(id+"F0.wireOp",EDGE,"E8.30.4"),sQuery(id+"F0.wireOp",EDGE,"E8.30.5"),sQuery(id+"F0.wireOp",EDGE,"E8.31.0"),sQuery(id+"F0.wireOp",EDGE,"E8.31.1"),sQuery(id+"F0.wireOp",EDGE,"E8.31.2"),sQuery(id+"F0.wireOp",EDGE,"E8.31.3"),sQuery(id+"F0.wireOp",EDGE,"E8.31.4"),sQuery(id+"F0.wireOp",EDGE,"E8.31.5"),sQuery(id+"F0.wireOp",EDGE,"E8.32.0"),sQuery(id+"F0.wireOp",EDGE,"E8.32.1"),sQuery(id+"F0.wireOp",EDGE,"E8.32.2"),sQuery(id+"F0.wireOp",EDGE,"E8.32.3"),sQuery(id+"F0.wireOp",EDGE,"E8.32.4"),sQuery(id+"F0.wireOp",EDGE,"E8.32.5"),sQuery(id+"F0.wireOp",EDGE,"E8.33.0"),sQuery(id+"F0.wireOp",EDGE,"E8.33.1"),sQuery(id+"F0.wireOp",EDGE,"E8.33.2"),sQuery(id+"F0.wireOp",EDGE,"E8.33.3"),sQuery(id+"F0.wireOp",EDGE,"E8.33.4"),sQuery(id+"F0.wireOp",EDGE,"E8.33.5"),sQuery(id+"F0.wireOp",EDGE,"E8.34.0"),sQuery(id+"F0.wireOp",EDGE,"E8.34.1"),sQuery(id+"F0.wireOp",EDGE,"E8.34.2"),sQuery(id+"F0.wireOp",EDGE,"E8.34.3"),sQuery(id+"F0.wireOp",EDGE,"E8.34.4"),sQuery(id+"F0.wireOp",EDGE,"E8.34.5"),sQuery(id+"F0.wireOp",EDGE,"E8.35.0"),sQuery(id+"F0.wireOp",EDGE,"E8.35.1"),sQuery(id+"F0.wireOp",EDGE,"E8.35.2"),sQuery(id+"F0.wireOp",EDGE,"E8.35.3"),sQuery(id+"F0.wireOp",EDGE,"E8.35.4"),sQuery(id+"F0.wireOp",EDGE,"E8.35.5"),sQuery(id+"F0.wireOp",EDGE,"E8.36.0"),sQuery(id+"F0.wireOp",EDGE,"E8.36.1"),sQuery(id+"F0.wireOp",EDGE,"E8.36.2"),sQuery(id+"F0.wireOp",EDGE,"E8.36.3"),sQuery(id+"F0.wireOp",EDGE,"E8.36.4"),sQuery(id+"F0.wireOp",EDGE,"E8.36.5"),sQuery(id+"F0.wireOp",EDGE,"E8.37.0"),sQuery(id+"F0.wireOp",EDGE,"E8.37.1"),sQuery(id+"F0.wireOp",EDGE,"E8.37.2"),sQuery(id+"F0.wireOp",EDGE,"E8.37.3"),sQuery(id+"F0.wireOp",EDGE,"E8.37.4"),sQuery(id+"F0.wireOp",EDGE,"E8.37.5"),sQuery(id+"F0.wireOp",EDGE,"E8.38.0"),sQuery(id+"F0.wireOp",EDGE,"E8.38.1"),sQuery(id+"F0.wireOp",EDGE,"E8.38.2"),sQuery(id+"F0.wireOp",EDGE,"E8.38.3"),sQuery(id+"F0.wireOp",EDGE,"E8.38.4"),sQuery(id+"F0.wireOp",EDGE,"E8.38.5"),sQuery(id+"F0.wireOp",EDGE,"E8.39.0"),sQuery(id+"F0.wireOp",EDGE,"E8.39.1"),sQuery(id+"F0.wireOp",EDGE,"E8.39.2"),sQuery(id+"F0.wireOp",EDGE,"E8.39.3"),sQuery(id+"F0.wireOp",EDGE,"E8.39.4"),sQuery(id+"F0.wireOp",EDGE,"E8.39.5"),sQuery(id+"F0.wireOp",EDGE,"E8.40.0"),sQuery(id+"F0.wireOp",EDGE,"E8.40.1"),sQuery(id+"F0.wireOp",EDGE,"E8.40.2"),sQuery(id+"F0.wireOp",EDGE,"E8.40.3"),sQuery(id+"F0.wireOp",EDGE,"E8.40.4"),sQuery(id+"F0.wireOp",EDGE,"E8.40.5"),sQuery(id+"F0.wireOp",EDGE,"E8.41.0"),sQuery(id+"F0.wireOp",EDGE,"E8.41.1"),sQuery(id+"F0.wireOp",EDGE,"E8.41.2"),sQuery(id+"F0.wireOp",EDGE,"E8.41.3"),sQuery(id+"F0.wireOp",EDGE,"E8.41.4"),sQuery(id+"F0.wireOp",EDGE,"E8.41.5"),sQuery(id+"F0.wireOp",EDGE,"E8.42.0"),sQuery(id+"F0.wireOp",EDGE,"E8.42.1"),sQuery(id+"F0.wireOp",EDGE,"E8.42.2"),sQuery(id+"F0.wireOp",EDGE,"E8.42.3"),sQuery(id+"F0.wireOp",EDGE,"E8.42.4"),sQuery(id+"F0.wireOp",EDGE,"E8.42.5"),sQuery(id+"F0.wireOp",EDGE,"E8.43.0"),sQuery(id+"F0.wireOp",EDGE,"E8.43.1"),sQuery(id+"F0.wireOp",EDGE,"E8.43.2"),sQuery(id+"F0.wireOp",EDGE,"E8.43.3"),sQuery(id+"F0.wireOp",EDGE,"E8.43.4"),sQuery(id+"F0.wireOp",EDGE,"E8.43.5"),sQuery(id+"F0.wireOp",EDGE,"E8.44.0"),sQuery(id+"F0.wireOp",EDGE,"E8.44.1"),sQuery(id+"F0.wireOp",EDGE,"E8.44.2"),sQuery(id+"F0.wireOp",EDGE,"E8.44.3"),sQuery(id+"F0.wireOp",EDGE,"E8.44.4"),sQuery(id+"F0.wireOp",EDGE,"E8.44.5"),sQuery(id+"F0.wireOp",EDGE,"E8.45.0"),sQuery(id+"F0.wireOp",EDGE,"E8.45.1"),sQuery(id+"F0.wireOp",EDGE,"E8.45.2"),sQuery(id+"F0.wireOp",EDGE,"E8.45.3"),sQuery(id+"F0.wireOp",EDGE,"E8.45.4"),sQuery(id+"F0.wireOp",EDGE,"E8.45.5"),sQuery(id+"F0.wireOp",EDGE,"E8.46.0"),sQuery(id+"F0.wireOp",EDGE,"E8.46.1"),sQuery(id+"F0.wireOp",EDGE,"E8.46.2"),sQuery(id+"F0.wireOp",EDGE,"E8.46.3"),sQuery(id+"F0.wireOp",EDGE,"E8.46.4"),sQuery(id+"F0.wireOp",EDGE,"E8.46.5"),sQuery(id+"F0.wireOp",EDGE,"E8.47.0"),sQuery(id+"F0.wireOp",EDGE,"E8.47.1"),sQuery(id+"F0.wireOp",EDGE,"E8.47.2"),sQuery(id+"F0.wireOp",EDGE,"E8.47.3"),sQuery(id+"F0.wireOp",EDGE,"E8.47.4"),sQuery(id+"F0.wireOp",EDGE,"E8.47.5"),sQuery(id+"F0.wireOp",EDGE,"E8.48.0"),sQuery(id+"F0.wireOp",EDGE,"E8.48.1"),sQuery(id+"F0.wireOp",EDGE,"E8.48.2"),sQuery(id+"F0.wireOp",EDGE,"E8.48.3"),sQuery(id+"F0.wireOp",EDGE,"E8.48.4"),sQuery(id+"F0.wireOp",EDGE,"E8.48.5"),sQuery(id+"F0.wireOp",EDGE,"E8.49.0"),sQuery(id+"F0.wireOp",EDGE,"E8.49.1"),sQuery(id+"F0.wireOp",EDGE,"E8.49.2"),sQuery(id+"F0.wireOp",EDGE,"E8.49.3"),sQuery(id+"F0.wireOp",EDGE,"E8.49.4"),sQuery(id+"F0.wireOp",EDGE,"E8.49.5"),sQuery(id+"F0.wireOp",EDGE,"E8.50.0"),sQuery(id+"F0.wireOp",EDGE,"E8.50.1"),sQuery(id+"F0.wireOp",EDGE,"E8.50.2"),sQuery(id+"F0.wireOp",EDGE,"E8.50.3"),sQuery(id+"F0.wireOp",EDGE,"E8.50.4"),sQuery(id+"F0.wireOp",EDGE,"E8.50.5"),sQuery(id+"F0.wireOp",EDGE,"E8.51.0"),sQuery(id+"F0.wireOp",EDGE,"E8.51.1"),sQuery(id+"F0.wireOp",EDGE,"E8.51.2"),sQuery(id+"F0.wireOp",EDGE,"E8.51.3"),sQuery(id+"F0.wireOp",EDGE,"E8.51.4"),sQuery(id+"F0.wireOp",EDGE,"E8.51.5"),sQuery(id+"F0.wireOp",EDGE,"E8.52.0"),sQuery(id+"F0.wireOp",EDGE,"E8.52.1"),sQuery(id+"F0.wireOp",EDGE,"E8.52.2"),sQuery(id+"F0.wireOp",EDGE,"E8.52.3"),sQuery(id+"F0.wireOp",EDGE,"E8.52.4"),sQuery(id+"F0.wireOp",EDGE,"E8.52.5"),sQuery(id+"F0.wireOp",EDGE,"E8.53.0"),sQuery(id+"F0.wireOp",EDGE,"E8.53.1"),sQuery(id+"F0.wireOp",EDGE,"E8.53.2"),sQuery(id+"F0.wireOp",EDGE,"E8.53.3"),sQuery(id+"F0.wireOp",EDGE,"E8.53.4"),sQuery(id+"F0.wireOp",EDGE,"E8.53.5"),sQuery(id+"F0.wireOp",EDGE,"E8.54.0"),sQuery(id+"F0.wireOp",EDGE,"E8.54.1"),sQuery(id+"F0.wireOp",EDGE,"E8.54.2"),sQuery(id+"F0.wireOp",EDGE,"E8.54.3"),sQuery(id+"F0.wireOp",EDGE,"E8.54.4"),sQuery(id+"F0.wireOp",EDGE,"E8.54.5"),sQuery(id+"F0.wireOp",EDGE,"E8.55.0"),sQuery(id+"F0.wireOp",EDGE,"E8.55.1"),sQuery(id+"F0.wireOp",EDGE,"E8.55.2"),sQuery(id+"F0.wireOp",EDGE,"E8.55.3"),sQuery(id+"F0.wireOp",EDGE,"E8.55.4"),sQuery(id+"F0.wireOp",EDGE,"E8.55.5"),sQuery(id+"F0.wireOp",EDGE,"E8.56.0"),sQuery(id+"F0.wireOp",EDGE,"E8.56.1"),sQuery(id+"F0.wireOp",EDGE,"E8.56.2"),sQuery(id+"F0.wireOp",EDGE,"E8.56.3"),sQuery(id+"F0.wireOp",EDGE,"E8.56.4"),sQuery(id+"F0.wireOp",EDGE,"E8.56.5"),sQuery(id+"F0.wireOp",EDGE,"E8.57.0"),sQuery(id+"F0.wireOp",EDGE,"E8.57.1"),sQuery(id+"F0.wireOp",EDGE,"E8.57.2"),sQuery(id+"F0.wireOp",EDGE,"E8.57.3"),sQuery(id+"F0.wireOp",EDGE,"E8.57.4"),sQuery(id+"F0.wireOp",EDGE,"E8.57.5"),sQuery(id+"F0.wireOp",EDGE,"E8.58.0"),sQuery(id+"F0.wireOp",EDGE,"E8.58.1"),sQuery(id+"F0.wireOp",EDGE,"E8.58.2"),sQuery(id+"F0.wireOp",EDGE,"E8.58.3"),sQuery(id+"F0.wireOp",EDGE,"E8.58.4"),sQuery(id+"F0.wireOp",EDGE,"E8.58.5"),sQuery(id+"F0.wireOp",EDGE,"E8.59.0"),sQuery(id+"F0.wireOp",EDGE,"E8.59.1"),sQuery(id+"F0.wireOp",EDGE,"E8.59.2"),sQuery(id+"F0.wireOp",EDGE,"E8.59.3"),sQuery(id+"F0.wireOp",EDGE,"E8.59.4"),sQuery(id+"F0.wireOp",EDGE,"E8.59.5"),sQuery(id+"F0.wireOp",EDGE,"E8.60.0"),sQuery(id+"F0.wireOp",EDGE,"E8.60.1"),sQuery(id+"F0.wireOp",EDGE,"E8.60.2"),sQuery(id+"F0.wireOp",EDGE,"E8.60.3"),sQuery(id+"F0.wireOp",EDGE,"E8.60.4"),sQuery(id+"F0.wireOp",EDGE,"E8.60.5"),sQuery(id+"F0.wireOp",EDGE,"E8.61.0"),sQuery(id+"F0.wireOp",EDGE,"E8.61.1"),sQuery(id+"F0.wireOp",EDGE,"E8.61.2"),sQuery(id+"F0.wireOp",EDGE,"E8.61.3"),sQuery(id+"F0.wireOp",EDGE,"E8.61.4"),sQuery(id+"F0.wireOp",EDGE,"E8.61.5"),sQuery(id+"F0.wireOp",EDGE,"E8.62.0"),sQuery(id+"F0.wireOp",EDGE,"E8.62.1"),sQuery(id+"F0.wireOp",EDGE,"E8.62.2"),sQuery(id+"F0.wireOp",EDGE,"E8.62.3"),sQuery(id+"F0.wireOp",EDGE,"E8.62.4"),sQuery(id+"F0.wireOp",EDGE,"E8.62.5"),sQuery(id+"F0.wireOp",EDGE,"E8.63.0"),sQuery(id+"F0.wireOp",EDGE,"E8.63.1"),sQuery(id+"F0.wireOp",EDGE,"E8.63.2"),sQuery(id+"F0.wireOp",EDGE,"E8.63.3"),sQuery(id+"F0.wireOp",EDGE,"E8.63.4"),sQuery(id+"F0.wireOp",EDGE,"E8.63.5"),sQuery(id+"F0.wireOp",EDGE,"E8.64.0"),sQuery(id+"F0.wireOp",EDGE,"E8.64.1"),sQuery(id+"F0.wireOp",EDGE,"E8.64.2"),sQuery(id+"F0.wireOp",EDGE,"E8.64.3"),sQuery(id+"F0.wireOp",EDGE,"E8.64.4"),sQuery(id+"F0.wireOp",EDGE,"E8.64.5"),sQuery(id+"F0.wireOp",EDGE,"E8.65.0"),sQuery(id+"F0.wireOp",EDGE,"E8.65.1"),sQuery(id+"F0.wireOp",EDGE,"E8.65.2"),sQuery(id+"F0.wireOp",EDGE,"E8.65.3"),sQuery(id+"F0.wireOp",EDGE,"E8.65.4"),sQuery(id+"F0.wireOp",EDGE,"E8.65.5"),sQuery(id+"F0.wireOp",EDGE,"E8.66.0"),sQuery(id+"F0.wireOp",EDGE,"E8.66.1"),sQuery(id+"F0.wireOp",EDGE,"E8.66.2"),sQuery(id+"F0.wireOp",EDGE,"E8.66.3"),sQuery(id+"F0.wireOp",EDGE,"E8.66.4"),sQuery(id+"F0.wireOp",EDGE,"E8.66.5"),sQuery(id+"F0.wireOp",EDGE,"E8.67.0"),sQuery(id+"F0.wireOp",EDGE,"E8.67.1"),sQuery(id+"F0.wireOp",EDGE,"E8.67.2"),sQuery(id+"F0.wireOp",EDGE,"E8.67.3"),sQuery(id+"F0.wireOp",EDGE,"E8.67.4"),sQuery(id+"F0.wireOp",EDGE,"E8.67.5"),sQuery(id+"F0.wireOp",EDGE,"E8.68.0"),sQuery(id+"F0.wireOp",EDGE,"E8.68.1"),sQuery(id+"F0.wireOp",EDGE,"E8.68.2"),sQuery(id+"F0.wireOp",EDGE,"E8.68.3"),sQuery(id+"F0.wireOp",EDGE,"E8.68.4"),sQuery(id+"F0.wireOp",EDGE,"E8.68.5"),sQuery(id+"F0.wireOp",EDGE,"E8.69.0"),sQuery(id+"F0.wireOp",EDGE,"E8.69.1"),sQuery(id+"F0.wireOp",EDGE,"E8.69.2"),sQuery(id+"F0.wireOp",EDGE,"E8.69.3"),sQuery(id+"F0.wireOp",EDGE,"E8.69.4"),sQuery(id+"F0.wireOp",EDGE,"E8.69.5"),sQuery(id+"F0.wireOp",EDGE,"E8.70.0"),sQuery(id+"F0.wireOp",EDGE,"E8.70.1"),sQuery(id+"F0.wireOp",EDGE,"E8.70.2"),sQuery(id+"F0.wireOp",EDGE,"E8.70.3"),sQuery(id+"F0.wireOp",EDGE,"E8.70.4"),sQuery(id+"F0.wireOp",EDGE,"E8.70.5"),sQuery(id+"F0.wireOp",EDGE,"E8.71.0"),sQuery(id+"F0.wireOp",EDGE,"E8.71.1"),sQuery(id+"F0.wireOp",EDGE,"E8.71.2"),sQuery(id+"F0.wireOp",EDGE,"E8.71.3"),sQuery(id+"F0.wireOp",EDGE,"E8.71.4"),sQuery(id+"F0.wireOp",EDGE,"E8.71.5"),sQuery(id+"F0.wireOp",EDGE,"E8.72.0"),sQuery(id+"F0.wireOp",EDGE,"E8.72.1"),sQuery(id+"F0.wireOp",EDGE,"E8.72.2"),sQuery(id+"F0.wireOp",EDGE,"E8.72.3"),sQuery(id+"F0.wireOp",EDGE,"E8.72.4"),sQuery(id+"F0.wireOp",EDGE,"E8.72.5"),sQuery(id+"F0.wireOp",EDGE,"E8.73.0"),sQuery(id+"F0.wireOp",EDGE,"E8.73.1"),sQuery(id+"F0.wireOp",EDGE,"E8.73.2"),sQuery(id+"F0.wireOp",EDGE,"E8.73.3"),sQuery(id+"F0.wireOp",EDGE,"E8.73.4"),sQuery(id+"F0.wireOp",EDGE,"E8.73.5"),sQuery(id+"F0.wireOp",EDGE,"E8.74.0"),sQuery(id+"F0.wireOp",EDGE,"E8.74.1"),sQuery(id+"F0.wireOp",EDGE,"E8.74.2"),sQuery(id+"F0.wireOp",EDGE,"E8.74.3"),sQuery(id+"F0.wireOp",EDGE,"E8.74.4"),sQuery(id+"F0.wireOp",EDGE,"E8.74.5"),sQuery(id+"F0.wireOp",EDGE,"E8.75.0"),sQuery(id+"F0.wireOp",EDGE,"E8.75.1"),sQuery(id+"F0.wireOp",EDGE,"E8.75.2"),sQuery(id+"F0.wireOp",EDGE,"E8.75.3"),sQuery(id+"F0.wireOp",EDGE,"E8.75.4"),sQuery(id+"F0.wireOp",EDGE,"E8.75.5"),sQuery(id+"F0.wireOp",EDGE,"E8.76.0"),sQuery(id+"F0.wireOp",EDGE,"E8.76.1"),sQuery(id+"F0.wireOp",EDGE,"E8.76.2"),sQuery(id+"F0.wireOp",EDGE,"E8.76.3"),sQuery(id+"F0.wireOp",EDGE,"E8.76.4"),sQuery(id+"F0.wireOp",EDGE,"E8.76.5"),sQuery(id+"F0.wireOp",EDGE,"E8.77.0"),sQuery(id+"F0.wireOp",EDGE,"E8.77.1"),sQuery(id+"F0.wireOp",EDGE,"E8.77.2"),sQuery(id+"F0.wireOp",EDGE,"E8.77.3"),sQuery(id+"F0.wireOp",EDGE,"E8.77.4"),sQuery(id+"F0.wireOp",EDGE,"E8.77.5"),sQuery(id+"F0.wireOp",EDGE,"E8.78.0"),sQuery(id+"F0.wireOp",EDGE,"E8.78.1"),sQuery(id+"F0.wireOp",EDGE,"E8.78.2"),sQuery(id+"F0.wireOp",EDGE,"E8.78.3"),sQuery(id+"F0.wireOp",EDGE,"E8.78.4"),sQuery(id+"F0.wireOp",EDGE,"E8.78.5"),sQuery(id+"F0.wireOp",EDGE,"E8.79.0"),sQuery(id+"F0.wireOp",EDGE,"E8.79.1"),sQuery(id+"F0.wireOp",EDGE,"E8.79.2"),sQuery(id+"F0.wireOp",EDGE,"E8.79.3"),sQuery(id+"F0.wireOp",EDGE,"E8.79.4"),sQuery(id+"F0.wireOp",EDGE,"E8.79.5"),sQuery(id+"F0.wireOp",EDGE,"E8.80.0"),sQuery(id+"F0.wireOp",EDGE,"E8.80.1"),sQuery(id+"F0.wireOp",EDGE,"E8.80.2"),sQuery(id+"F0.wireOp",EDGE,"E8.80.3"),sQuery(id+"F0.wireOp",EDGE,"E8.80.4"),sQuery(id+"F0.wireOp",EDGE,"E8.80.5"),sQuery(id+"F0.wireOp",EDGE,"E8.81.0"),sQuery(id+"F0.wireOp",EDGE,"E8.81.1"),sQuery(id+"F0.wireOp",EDGE,"E8.81.2"),sQuery(id+"F0.wireOp",EDGE,"E8.81.3"),sQuery(id+"F0.wireOp",EDGE,"E8.81.4"),sQuery(id+"F0.wireOp",EDGE,"E8.81.5"),sQuery(id+"F0.wireOp",EDGE,"E8.82.0"),sQuery(id+"F0.wireOp",EDGE,"E8.82.1"),sQuery(id+"F0.wireOp",EDGE,"E8.82.2"),sQuery(id+"F0.wireOp",EDGE,"E8.82.3"),sQuery(id+"F0.wireOp",EDGE,"E8.82.4"),sQuery(id+"F0.wireOp",EDGE,"E8.82.5"),sQuery(id+"F0.wireOp",EDGE,"E8.83.0"),sQuery(id+"F0.wireOp",EDGE,"E8.83.1"),sQuery(id+"F0.wireOp",EDGE,"E8.83.2"),sQuery(id+"F0.wireOp",EDGE,"E8.83.3"),sQuery(id+"F0.wireOp",EDGE,"E8.83.4"),sQuery(id+"F0.wireOp",EDGE,"E8.83.5"),sQuery(id+"F0.wireOp",EDGE,"E8.84.0"),sQuery(id+"F0.wireOp",EDGE,"E8.84.1"),sQuery(id+"F0.wireOp",EDGE,"E8.84.2"),sQuery(id+"F0.wireOp",EDGE,"E8.84.3"),sQuery(id+"F0.wireOp",EDGE,"E8.84.4"),sQuery(id+"F0.wireOp",EDGE,"E8.84.5"),sQuery(id+"F0.wireOp",EDGE,"E8.85.0"),sQuery(id+"F0.wireOp",EDGE,"E8.85.1"),sQuery(id+"F0.wireOp",EDGE,"E8.85.2"),sQuery(id+"F0.wireOp",EDGE,"E8.85.3"),sQuery(id+"F0.wireOp",EDGE,"E8.85.4"),sQuery(id+"F0.wireOp",EDGE,"E8.85.5"),sQuery(id+"F0.wireOp",EDGE,"E8.86.0"),sQuery(id+"F0.wireOp",EDGE,"E8.86.1"),sQuery(id+"F0.wireOp",EDGE,"E8.86.2"),sQuery(id+"F0.wireOp",EDGE,"E8.86.3"),sQuery(id+"F0.wireOp",EDGE,"E8.86.4"),sQuery(id+"F0.wireOp",EDGE,"E8.86.5"),sQuery(id+"F0.wireOp",EDGE,"E8.87.0"),sQuery(id+"F0.wireOp",EDGE,"E8.87.1"),sQuery(id+"F0.wireOp",EDGE,"E8.87.2"),sQuery(id+"F0.wireOp",EDGE,"E8.87.3"),sQuery(id+"F0.wireOp",EDGE,"E8.87.4"),sQuery(id+"F0.wireOp",EDGE,"E8.87.5"),sQuery(id+"F0.wireOp",EDGE,"E8.88.0"),sQuery(id+"F0.wireOp",EDGE,"E8.88.1"),sQuery(id+"F0.wireOp",EDGE,"E8.88.2"),sQuery(id+"F0.wireOp",EDGE,"E8.88.3"),sQuery(id+"F0.wireOp",EDGE,"E8.88.4"),sQuery(id+"F0.wireOp",EDGE,"E8.88.5"),sQuery(id+"F0.wireOp",EDGE,"E8.89.0"),sQuery(id+"F0.wireOp",EDGE,"E8.89.1"),sQuery(id+"F0.wireOp",EDGE,"E8.89.2"),sQuery(id+"F0.wireOp",EDGE,"E8.89.3"),sQuery(id+"F0.wireOp",EDGE,"E8.89.4"),sQuery(id+"F0.wireOp",EDGE,"E8.89.5"),sQuery(id+"F0.wireOp",EDGE,"E8.90.0"),sQuery(id+"F0.wireOp",EDGE,"E8.90.1"),sQuery(id+"F0.wireOp",EDGE,"E8.90.2"),sQuery(id+"F0.wireOp",EDGE,"E8.90.3"),sQuery(id+"F0.wireOp",EDGE,"E8.90.4"),sQuery(id+"F0.wireOp",EDGE,"E8.90.5"),sQuery(id+"F0.wireOp",EDGE,"E8.91.0"),sQuery(id+"F0.wireOp",EDGE,"E8.91.1"),sQuery(id+"F0.wireOp",EDGE,"E8.91.2"),sQuery(id+"F0.wireOp",EDGE,"E8.91.3"),sQuery(id+"F0.wireOp",EDGE,"E8.91.4"),sQuery(id+"F0.wireOp",EDGE,"E8.91.5"),sQuery(id+"F0.wireOp",EDGE,"E8.92.0"),sQuery(id+"F0.wireOp",EDGE,"E8.92.1"),sQuery(id+"F0.wireOp",EDGE,"E8.92.2"),sQuery(id+"F0.wireOp",EDGE,"E8.92.3"),sQuery(id+"F0.wireOp",EDGE,"E8.92.4"),sQuery(id+"F0.wireOp",EDGE,"E8.92.5"),sQuery(id+"F0.wireOp",EDGE,"E8.93.0"),sQuery(id+"F0.wireOp",EDGE,"E8.93.1"),sQuery(id+"F0.wireOp",EDGE,"E8.93.2"),sQuery(id+"F0.wireOp",EDGE,"E8.93.3"),sQuery(id+"F0.wireOp",EDGE,"E8.93.4"),sQuery(id+"F0.wireOp",EDGE,"E8.93.5"),sQuery(id+"F0.wireOp",EDGE,"E8.94.0"),sQuery(id+"F0.wireOp",EDGE,"E8.94.1"),sQuery(id+"F0.wireOp",EDGE,"E8.94.2"),sQuery(id+"F0.wireOp",EDGE,"E8.94.3"),sQuery(id+"F0.wireOp",EDGE,"E8.94.4"),sQuery(id+"F0.wireOp",EDGE,"E8.94.5"),sQuery(id+"F0.wireOp",EDGE,"E8.95.0"),sQuery(id+"F0.wireOp",EDGE,"E8.95.1"),sQuery(id+"F0.wireOp",EDGE,"E8.95.2"),sQuery(id+"F0.wireOp",EDGE,"E8.95.3"),sQuery(id+"F0.wireOp",EDGE,"E8.95.4"),sQuery(id+"F0.wireOp",EDGE,"E8.95.5"),sQuery(id+"F0.wireOp",EDGE,"E8.96.0"),sQuery(id+"F0.wireOp",EDGE,"E8.96.1"),sQuery(id+"F0.wireOp",EDGE,"E8.96.2"),sQuery(id+"F0.wireOp",EDGE,"E8.96.3"),sQuery(id+"F0.wireOp",EDGE,"E8.96.4"),sQuery(id+"F0.wireOp",EDGE,"E8.96.5"),sQuery(id+"F0.wireOp",EDGE,"E8.97.0"),sQuery(id+"F0.wireOp",EDGE,"E8.97.1"),sQuery(id+"F0.wireOp",EDGE,"E8.97.2"),sQuery(id+"F0.wireOp",EDGE,"E8.97.3"),sQuery(id+"F0.wireOp",EDGE,"E8.97.4"),sQuery(id+"F0.wireOp",EDGE,"E8.97.5")])],"isStart":false});
            var sketch = newSketch(context, id + "F4", { "sketchPlane" : qUnion([Q0])});
            skCircle(sketch, "E10", {"center": v(0, 7) * mm, "radius": 3.9 * mm});
            skSolve(sketch);
        }
        {
            var Q0;
            Q0 = qSketchRegion(id + "F4", true);
            extrude(context, id + "F5", {"entities" : qUnion([Q0]), "operationType" : NewBodyOperationType.ADD, "depth" : .1 * mm, "offsetDistance" : 25 * mm});
        }
    });
